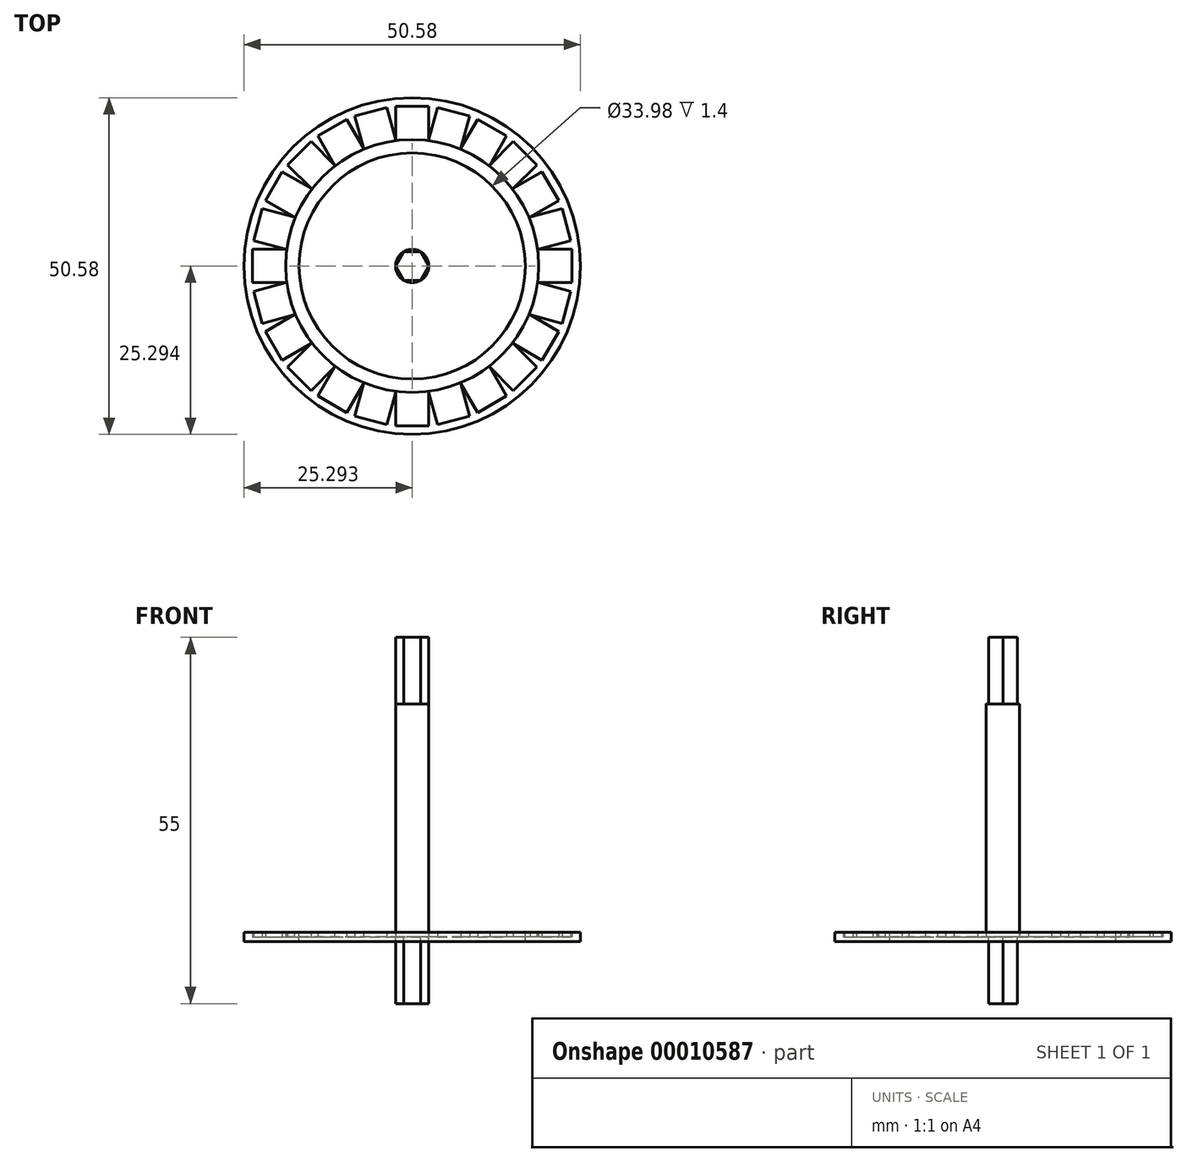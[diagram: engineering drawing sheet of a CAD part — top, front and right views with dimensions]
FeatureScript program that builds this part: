
annotation { "Feature Type Name" : "Feature", "Feature Type Description" : "" }
export const myFeature = defineFeature(function(context is Context, id is Id, definition is map)
    precondition{}
    {
        {
            var Q0;
            Q0=qCreatedBy(makeId("Top.planeOp"),FACE);
            var sketch = newSketch(context, id + "F0", { "sketchPlane" : qUnion([Q0])});
            skCircle(sketch, "E0", {"center": v(-14.89, 0.25) * mm, "radius": 18.99 * mm});
            skPoint(sketch, "E1", {"position": v(-14.89, 19.24) * mm});
            skLineSegment(sketch, "E2.bottom", {"start": v(-17.39, 24.24) * mm, "end": v(-12.39, 24.24) * mm});
            skLineSegment(sketch, "E2.top", {"start": v(-17.39, 19.24) * mm, "end": v(-12.39, 19.24) * mm});
            skLineSegment(sketch, "E2.left", {"start": v(-17.39, 24.24) * mm, "end": v(-17.39, 19.24) * mm});
            skLineSegment(sketch, "E2.right", {"start": v(-12.39, 24.24) * mm, "end": v(-12.39, 19.24) * mm});
            skPoint(sketch, "E3.1.0", {"position": v(-16.97, 18.97) * mm});
            skPoint(sketch, "E3.2.0", {"position": v(-18.92, 18.16) * mm});
            skPoint(sketch, "E3.3.0", {"position": v(-20.59, 16.88) * mm});
            skPoint(sketch, "E3.4.0", {"position": v(-21.87, 15.21) * mm});
            skPoint(sketch, "E3.5.0", {"position": v(-22.67, 13.27) * mm});
            skPoint(sketch, "E3.6.0", {"position": v(-22.95, 11.18) * mm});
            skPoint(sketch, "E3.7.0", {"position": v(-22.67, 9.1) * mm});
            skPoint(sketch, "E3.8.0", {"position": v(-21.87, 7.15) * mm});
            skPoint(sketch, "E3.9.0", {"position": v(-20.59, 5.48) * mm});
            skPoint(sketch, "E3.10.0", {"position": v(-18.92, 4.2) * mm});
            skPoint(sketch, "E3.11.0", {"position": v(-16.97, 3.4) * mm});
            skPoint(sketch, "E3.12.0", {"position": v(-14.89, 3.12) * mm});
            skPoint(sketch, "E3.13.0", {"position": v(-12.8, 3.4) * mm});
            skPoint(sketch, "E3.14.0", {"position": v(-10.86, 4.2) * mm});
            skPoint(sketch, "E3.15.0", {"position": v(-9.19, 5.48) * mm});
            skPoint(sketch, "E3.16.0", {"position": v(-7.9, 7.15) * mm});
            skPoint(sketch, "E3.17.0", {"position": v(-7.1, 9.1) * mm});
            skPoint(sketch, "E3.18.0", {"position": v(-6.82, 11.18) * mm});
            skPoint(sketch, "E3.19.0", {"position": v(-7.1, 13.27) * mm});
            skPoint(sketch, "E3.20.0", {"position": v(-7.9, 15.21) * mm});
            skPoint(sketch, "E3.21.0", {"position": v(-9.19, 16.88) * mm});
            skPoint(sketch, "E3.22.0", {"position": v(-10.86, 18.16) * mm});
            skPoint(sketch, "E3.23.0", {"position": v(-12.8, 18.97) * mm});
            skPoint(sketch, "E3.center", {"position": v(-14.89, 11.18) * mm});
            skLineSegment(sketch, "E4.1.0", {"start": v(-23.51, 22.78) * mm, "end": v(-22.22, 17.95) * mm});
            skLineSegment(sketch, "E4.1.1", {"start": v(-18.68, 24.07) * mm, "end": v(-17.39, 19.24) * mm});
            skLineSegment(sketch, "E4.1.2", {"start": v(-23.51, 22.78) * mm, "end": v(-18.68, 24.07) * mm});
            skLineSegment(sketch, "E4.1.3", {"start": v(-22.22, 17.95) * mm, "end": v(-17.39, 19.24) * mm});
            skLineSegment(sketch, "E4.2.0", {"start": v(-29.05, 19.78) * mm, "end": v(-26.55, 15.45) * mm});
            skLineSegment(sketch, "E4.2.1", {"start": v(-24.72, 22.28) * mm, "end": v(-22.22, 17.95) * mm});
            skLineSegment(sketch, "E4.2.2", {"start": v(-29.05, 19.78) * mm, "end": v(-24.72, 22.28) * mm});
            skLineSegment(sketch, "E4.2.3", {"start": v(-26.55, 15.45) * mm, "end": v(-22.22, 17.95) * mm});
            skLineSegment(sketch, "E4.3.0", {"start": v(-33.62, 15.45) * mm, "end": v(-30.08, 11.91) * mm});
            skLineSegment(sketch, "E4.3.1", {"start": v(-30.08, 18.98) * mm, "end": v(-26.55, 15.45) * mm});
            skLineSegment(sketch, "E4.3.2", {"start": v(-33.62, 15.45) * mm, "end": v(-30.08, 18.98) * mm});
            skLineSegment(sketch, "E4.3.3", {"start": v(-30.08, 11.91) * mm, "end": v(-26.55, 15.45) * mm});
            skLineSegment(sketch, "E4.4.0", {"start": v(-36.91, 10.08) * mm, "end": v(-32.58, 7.58) * mm});
            skLineSegment(sketch, "E4.4.1", {"start": v(-34.41, 14.41) * mm, "end": v(-30.08, 11.91) * mm});
            skLineSegment(sketch, "E4.4.2", {"start": v(-36.91, 10.08) * mm, "end": v(-34.41, 14.41) * mm});
            skLineSegment(sketch, "E4.4.3", {"start": v(-32.58, 7.58) * mm, "end": v(-30.08, 11.91) * mm});
            skLineSegment(sketch, "E4.5.0", {"start": v(-38.7, 4.05) * mm, "end": v(-33.88, 2.75) * mm});
            skLineSegment(sketch, "E4.5.1", {"start": v(-37.41, 8.88) * mm, "end": v(-32.58, 7.58) * mm});
            skLineSegment(sketch, "E4.5.2", {"start": v(-38.7, 4.05) * mm, "end": v(-37.41, 8.88) * mm});
            skLineSegment(sketch, "E4.5.3", {"start": v(-33.88, 2.75) * mm, "end": v(-32.58, 7.58) * mm});
            skLineSegment(sketch, "E4.6.0", {"start": v(-38.88, -2.25) * mm, "end": v(-33.88, -2.25) * mm});
            skLineSegment(sketch, "E4.6.1", {"start": v(-38.88, 2.75) * mm, "end": v(-33.88, 2.75) * mm});
            skLineSegment(sketch, "E4.6.2", {"start": v(-38.88, -2.25) * mm, "end": v(-38.88, 2.75) * mm});
            skLineSegment(sketch, "E4.6.3", {"start": v(-33.88, -2.25) * mm, "end": v(-33.88, 2.75) * mm});
            skLineSegment(sketch, "E4.7.0", {"start": v(-37.41, -8.37) * mm, "end": v(-32.58, -7.08) * mm});
            skLineSegment(sketch, "E4.7.1", {"start": v(-38.7, -3.54) * mm, "end": v(-33.88, -2.25) * mm});
            skLineSegment(sketch, "E4.7.2", {"start": v(-37.41, -8.37) * mm, "end": v(-38.7, -3.54) * mm});
            skLineSegment(sketch, "E4.7.3", {"start": v(-32.58, -7.08) * mm, "end": v(-33.88, -2.25) * mm});
            skLineSegment(sketch, "E4.8.0", {"start": v(-34.41, -13.9) * mm, "end": v(-30.08, -11.4) * mm});
            skLineSegment(sketch, "E4.8.1", {"start": v(-36.91, -9.58) * mm, "end": v(-32.58, -7.08) * mm});
            skLineSegment(sketch, "E4.8.2", {"start": v(-34.41, -13.9) * mm, "end": v(-36.91, -9.58) * mm});
            skLineSegment(sketch, "E4.8.3", {"start": v(-30.08, -11.4) * mm, "end": v(-32.58, -7.08) * mm});
            skLineSegment(sketch, "E4.9.0", {"start": v(-30.08, -18.48) * mm, "end": v(-26.55, -14.94) * mm});
            skLineSegment(sketch, "E4.9.1", {"start": v(-33.62, -14.94) * mm, "end": v(-30.08, -11.4) * mm});
            skLineSegment(sketch, "E4.9.2", {"start": v(-30.08, -18.48) * mm, "end": v(-33.62, -14.94) * mm});
            skLineSegment(sketch, "E4.9.3", {"start": v(-26.55, -14.94) * mm, "end": v(-30.08, -11.4) * mm});
            skLineSegment(sketch, "E4.10.0", {"start": v(-24.72, -21.77) * mm, "end": v(-22.22, -17.44) * mm});
            skLineSegment(sketch, "E4.10.1", {"start": v(-29.05, -19.27) * mm, "end": v(-26.55, -14.94) * mm});
            skLineSegment(sketch, "E4.10.2", {"start": v(-24.72, -21.77) * mm, "end": v(-29.05, -19.27) * mm});
            skLineSegment(sketch, "E4.10.3", {"start": v(-22.22, -17.44) * mm, "end": v(-26.55, -14.94) * mm});
            skLineSegment(sketch, "E4.11.0", {"start": v(-18.68, -23.57) * mm, "end": v(-17.39, -18.74) * mm});
            skLineSegment(sketch, "E4.11.1", {"start": v(-23.51, -22.27) * mm, "end": v(-22.22, -17.44) * mm});
            skLineSegment(sketch, "E4.11.2", {"start": v(-18.68, -23.57) * mm, "end": v(-23.51, -22.27) * mm});
            skLineSegment(sketch, "E4.11.3", {"start": v(-17.39, -18.74) * mm, "end": v(-22.22, -17.44) * mm});
            skLineSegment(sketch, "E4.12.0", {"start": v(-12.39, -23.74) * mm, "end": v(-12.39, -18.74) * mm});
            skLineSegment(sketch, "E4.12.1", {"start": v(-17.39, -23.74) * mm, "end": v(-17.39, -18.74) * mm});
            skLineSegment(sketch, "E4.12.2", {"start": v(-12.39, -23.74) * mm, "end": v(-17.39, -23.74) * mm});
            skLineSegment(sketch, "E4.12.3", {"start": v(-12.39, -18.74) * mm, "end": v(-17.39, -18.74) * mm});
            skLineSegment(sketch, "E4.13.0", {"start": v(-6.26, -22.27) * mm, "end": v(-7.56, -17.44) * mm});
            skLineSegment(sketch, "E4.13.1", {"start": v(-11.1, -23.57) * mm, "end": v(-12.39, -18.74) * mm});
            skLineSegment(sketch, "E4.13.2", {"start": v(-6.26, -22.27) * mm, "end": v(-11.1, -23.57) * mm});
            skLineSegment(sketch, "E4.13.3", {"start": v(-7.56, -17.44) * mm, "end": v(-12.39, -18.74) * mm});
            skLineSegment(sketch, "E4.14.0", {"start": v(-0.73, -19.27) * mm, "end": v(-3.23, -14.94) * mm});
            skLineSegment(sketch, "E4.14.1", {"start": v(-5.06, -21.77) * mm, "end": v(-7.56, -17.44) * mm});
            skLineSegment(sketch, "E4.14.2", {"start": v(-0.73, -19.27) * mm, "end": v(-5.06, -21.77) * mm});
            skLineSegment(sketch, "E4.14.3", {"start": v(-3.23, -14.94) * mm, "end": v(-7.56, -17.44) * mm});
            skLineSegment(sketch, "E4.15.0", {"start": v(3.84, -14.94) * mm, "end": v(0.3, -11.4) * mm});
            skLineSegment(sketch, "E4.15.1", {"start": v(0.3, -18.48) * mm, "end": v(-3.23, -14.94) * mm});
            skLineSegment(sketch, "E4.15.2", {"start": v(3.84, -14.94) * mm, "end": v(0.3, -18.48) * mm});
            skLineSegment(sketch, "E4.15.3", {"start": v(0.3, -11.4) * mm, "end": v(-3.23, -14.94) * mm});
            skLineSegment(sketch, "E4.16.0", {"start": v(7.14, -9.58) * mm, "end": v(2.8, -7.08) * mm});
            skLineSegment(sketch, "E4.16.1", {"start": v(4.64, -13.9) * mm, "end": v(0.3, -11.4) * mm});
            skLineSegment(sketch, "E4.16.2", {"start": v(7.14, -9.58) * mm, "end": v(4.64, -13.9) * mm});
            skLineSegment(sketch, "E4.16.3", {"start": v(2.8, -7.08) * mm, "end": v(0.3, -11.4) * mm});
            skLineSegment(sketch, "E4.17.0", {"start": v(8.93, -3.54) * mm, "end": v(4.1, -2.25) * mm});
            skLineSegment(sketch, "E4.17.1", {"start": v(7.64, -8.37) * mm, "end": v(2.8, -7.08) * mm});
            skLineSegment(sketch, "E4.17.2", {"start": v(8.93, -3.54) * mm, "end": v(7.64, -8.37) * mm});
            skLineSegment(sketch, "E4.17.3", {"start": v(4.1, -2.25) * mm, "end": v(2.8, -7.08) * mm});
            skLineSegment(sketch, "E4.18.0", {"start": v(9.1, 2.75) * mm, "end": v(4.1, 2.75) * mm});
            skLineSegment(sketch, "E4.18.1", {"start": v(9.1, -2.25) * mm, "end": v(4.1, -2.25) * mm});
            skLineSegment(sketch, "E4.18.2", {"start": v(9.1, 2.75) * mm, "end": v(9.1, -2.25) * mm});
            skLineSegment(sketch, "E4.18.3", {"start": v(4.1, 2.75) * mm, "end": v(4.1, -2.25) * mm});
            skLineSegment(sketch, "E4.19.0", {"start": v(7.64, 8.88) * mm, "end": v(2.8, 7.58) * mm});
            skLineSegment(sketch, "E4.19.1", {"start": v(8.93, 4.05) * mm, "end": v(4.1, 2.75) * mm});
            skLineSegment(sketch, "E4.19.2", {"start": v(7.64, 8.88) * mm, "end": v(8.93, 4.05) * mm});
            skLineSegment(sketch, "E4.19.3", {"start": v(2.8, 7.58) * mm, "end": v(4.1, 2.75) * mm});
            skLineSegment(sketch, "E4.20.0", {"start": v(4.64, 14.41) * mm, "end": v(0.3, 11.91) * mm});
            skLineSegment(sketch, "E4.20.1", {"start": v(7.14, 10.08) * mm, "end": v(2.8, 7.58) * mm});
            skLineSegment(sketch, "E4.20.2", {"start": v(4.64, 14.41) * mm, "end": v(7.14, 10.08) * mm});
            skLineSegment(sketch, "E4.20.3", {"start": v(0.3, 11.91) * mm, "end": v(2.8, 7.58) * mm});
            skLineSegment(sketch, "E4.21.0", {"start": v(0.3, 18.98) * mm, "end": v(-3.23, 15.45) * mm});
            skLineSegment(sketch, "E4.21.1", {"start": v(3.84, 15.45) * mm, "end": v(0.3, 11.91) * mm});
            skLineSegment(sketch, "E4.21.2", {"start": v(0.3, 18.98) * mm, "end": v(3.84, 15.45) * mm});
            skLineSegment(sketch, "E4.21.3", {"start": v(-3.23, 15.45) * mm, "end": v(0.3, 11.91) * mm});
            skLineSegment(sketch, "E4.22.0", {"start": v(-5.06, 22.28) * mm, "end": v(-7.56, 17.95) * mm});
            skLineSegment(sketch, "E4.22.1", {"start": v(-0.73, 19.78) * mm, "end": v(-3.23, 15.45) * mm});
            skLineSegment(sketch, "E4.22.2", {"start": v(-5.06, 22.28) * mm, "end": v(-0.73, 19.78) * mm});
            skLineSegment(sketch, "E4.22.3", {"start": v(-7.56, 17.95) * mm, "end": v(-3.23, 15.45) * mm});
            skLineSegment(sketch, "E4.23.0", {"start": v(-11.1, 24.07) * mm, "end": v(-12.39, 19.24) * mm});
            skLineSegment(sketch, "E4.23.1", {"start": v(-6.26, 22.78) * mm, "end": v(-7.56, 17.95) * mm});
            skLineSegment(sketch, "E4.23.2", {"start": v(-11.1, 24.07) * mm, "end": v(-6.26, 22.78) * mm});
            skLineSegment(sketch, "E4.23.3", {"start": v(-12.39, 19.24) * mm, "end": v(-7.56, 17.95) * mm});
            skPoint(sketch, "E5", {"position": v(-38.88, 0.25) * mm});
            skPoint(sketch, "E6", {"position": v(9.1, 0.25) * mm});
            skCircle(sketch, "E7", {"center": v(-14.89, 0.25) * mm, "radius": 23.99 * mm});
            skCircle(sketch, "E8.0", {"center": v(-14.89, 0.25) * mm, "radius": 25.29 * mm});
            skCircle(sketch, "E9.0", {"center": v(-14.89, 0.25) * mm, "radius": 16.99 * mm});
            skLineSegment(sketch, "E10", {"start": v(-14.89, 3.12) * mm, "end": v(-14.89, 19.24) * mm});
            skCircle(sketch, "E11.cCircle", {"center": v(-14.89, 0.25) * mm, "radius": 2.17 * mm, "construction": true});
            skLineSegment(sketch, "E11.0", {"start": v(-13.64, -1.91) * mm, "end": v(-16.14, -1.91) * mm});
            skLineSegment(sketch, "E11.1", {"start": v(-16.14, -1.91) * mm, "end": v(-17.39, 0.25) * mm});
            skLineSegment(sketch, "E11.2", {"start": v(-17.39, 0.25) * mm, "end": v(-16.14, 2.42) * mm});
            skLineSegment(sketch, "E11.3", {"start": v(-16.14, 2.42) * mm, "end": v(-13.64, 2.42) * mm});
            skLineSegment(sketch, "E11.4", {"start": v(-13.64, 2.42) * mm, "end": v(-12.39, 0.25) * mm});
            skLineSegment(sketch, "E11.5", {"start": v(-12.39, 0.25) * mm, "end": v(-13.64, -1.91) * mm});
            skPoint(sketch, "E11.0.midPoint", {"position": v(-14.89, -1.91) * mm});
            skLineSegment(sketch, "E12.bottom", {"start": v(-40.18, 25.54) * mm, "end": v(10.4, 25.54) * mm});
            skLineSegment(sketch, "E12.top", {"start": v(-40.18, -25.04) * mm, "end": v(10.4, -25.04) * mm});
            skLineSegment(sketch, "E12.left", {"start": v(-40.18, 25.54) * mm, "end": v(-40.18, -25.04) * mm});
            skLineSegment(sketch, "E12.right", {"start": v(10.4, 25.54) * mm, "end": v(10.4, -25.04) * mm});
            skCircle(sketch, "E13", {"center": v(-14.89, 0.25) * mm, "radius": 2.5 * mm});
            skCircle(sketch, "E14.0", {"center": v(-14.89, 0.25) * mm, "radius": 26.79 * mm});
            skCircle(sketch, "E15", {"center": v(-40.18, 25.54) * mm, "radius": 1 * mm});
            skCircle(sketch, "E16", {"center": v(10.4, 25.54) * mm, "radius": 1 * mm});
            skCircle(sketch, "E17", {"center": v(-40.18, -25.04) * mm, "radius": 1 * mm});
            skCircle(sketch, "E18", {"center": v(10.4, -25.04) * mm, "radius": 1 * mm});
            skCircle(sketch, "E19.0", {"center": v(-40.18, 25.54) * mm, "radius": 3 * mm});
            skCircle(sketch, "E20", {"center": v(10.4, 25.54) * mm, "radius": 3 * mm});
            skCircle(sketch, "E21", {"center": v(10.4, -25.04) * mm, "radius": 3 * mm});
            skCircle(sketch, "E22", {"center": v(-40.18, -25.04) * mm, "radius": 3 * mm});
            skEllipse(sketch, "E23", {"center": v(-14.89, 11.18) * mm, "majorRadius": 6.02 * mm, "minorRadius": 3.34 * mm, "majorAxis": v(0, -1)});
            skEllipse(sketch, "E24.1.0", {"center": v(-23.43, 7.07) * mm, "majorRadius": 6.02 * mm, "minorRadius": 3.34 * mm, "majorAxis": v(0.78, -0.62)});
            skEllipse(sketch, "E24.2.0", {"center": v(-25.54, -2.18) * mm, "majorRadius": 6.02 * mm, "minorRadius": 3.34 * mm, "majorAxis": v(0.97, 0.22)});
            skEllipse(sketch, "E24.3.0", {"center": v(-19.63, -9.6) * mm, "majorRadius": 6.02 * mm, "minorRadius": 3.34 * mm, "majorAxis": v(0.43, 0.9)});
            skEllipse(sketch, "E24.4.0", {"center": v(-10.15, -9.6) * mm, "majorRadius": 6.02 * mm, "minorRadius": 3.34 * mm, "majorAxis": v(-0.43, 0.9)});
            skEllipse(sketch, "E24.5.0", {"center": v(-4.23, -2.18) * mm, "majorRadius": 6.02 * mm, "minorRadius": 3.34 * mm, "majorAxis": v(-0.97, 0.22)});
            skEllipse(sketch, "E24.6.0", {"center": v(-6.34, 7.07) * mm, "majorRadius": 6.02 * mm, "minorRadius": 3.34 * mm, "majorAxis": v(-0.78, -0.62)});
            skSolve(sketch);
        }
        {
            var Q0;
            Q0=makeQuery(id+"F0.imprint","IMPRINT",FACE,{"disambiguationData":[TD([[makeQuery(id+"F0.imprint","IMPRINT",EDGE,{"derivedFrom":sQuery(id+"F0.wireOp",EDGE,"E9.0")}),-1.0]])]});
            var Q1;
            {var subQ40=sQuery(id+"F0.wireOp",EDGE,"E2.left");var subQ122=sQuery(id+"F0.wireOp",EDGE,"E2.bottom");var subQ171=makeQuery(id+"F0.imprint","INTERSECT",VERTEX,{"derivedFrom":[subQ122,subQ40]});Q1=makeQuery(id+"F0.imprint","IMPRINT",FACE,{"disambiguationData":[TD([[makeQuery(id+"F0.imprint","IMPRINT",EDGE,{"disambiguationData":[TD([[subQ171,-1.0]])],"derivedFrom":subQ122}),1.0]])]});}
            var Q2;
            {var subQ0=sQuery(id+"F0.wireOp",EDGE,"E7");var subQ4=sQuery(id+"F0.wireOp",EDGE,"E4.12.1");var subQ5=makeQuery(id+"F0.imprint","INTERSECT",VERTEX,{"derivedFrom":[subQ4,subQ0]});Q2=makeQuery(id+"F0.imprint","IMPRINT",FACE,{"disambiguationData":[TD([[makeQuery(id+"F0.imprint","IMPRINT",EDGE,{"disambiguationData":[TD([[subQ5,-1.0]])],"derivedFrom":subQ0}),1.0]])]});}
            var Q3;
            {var subQ0=sQuery(id+"F0.wireOp",EDGE,"E7");var subQ4=sQuery(id+"F0.wireOp",EDGE,"E4.11.1");var subQ5=makeQuery(id+"F0.imprint","INTERSECT",VERTEX,{"derivedFrom":[subQ4,subQ0]});Q3=makeQuery(id+"F0.imprint","IMPRINT",FACE,{"disambiguationData":[TD([[makeQuery(id+"F0.imprint","IMPRINT",EDGE,{"disambiguationData":[TD([[subQ5,-1.0]])],"derivedFrom":subQ0}),1.0]])]});}
            var Q4;
            {var subQ0=sQuery(id+"F0.wireOp",EDGE,"E7");var subQ4=sQuery(id+"F0.wireOp",EDGE,"E4.13.1");var subQ5=makeQuery(id+"F0.imprint","INTERSECT",VERTEX,{"derivedFrom":[subQ4,subQ0]});Q4=makeQuery(id+"F0.imprint","IMPRINT",FACE,{"disambiguationData":[TD([[makeQuery(id+"F0.imprint","IMPRINT",EDGE,{"disambiguationData":[TD([[subQ5,-1.0]])],"derivedFrom":subQ0}),1.0]])]});}
            var Q5;
            {var subQ0=sQuery(id+"F0.wireOp",EDGE,"E7");var subQ4=sQuery(id+"F0.wireOp",EDGE,"E4.10.1");var subQ5=makeQuery(id+"F0.imprint","INTERSECT",VERTEX,{"derivedFrom":[subQ4,subQ0]});Q5=makeQuery(id+"F0.imprint","IMPRINT",FACE,{"disambiguationData":[TD([[makeQuery(id+"F0.imprint","IMPRINT",EDGE,{"disambiguationData":[TD([[subQ5,-1.0]])],"derivedFrom":subQ0}),1.0]])]});}
            var Q6;
            {var subQ0=sQuery(id+"F0.wireOp",EDGE,"E7");var subQ4=sQuery(id+"F0.wireOp",EDGE,"E4.14.1");var subQ5=makeQuery(id+"F0.imprint","INTERSECT",VERTEX,{"derivedFrom":[subQ4,subQ0]});Q6=makeQuery(id+"F0.imprint","IMPRINT",FACE,{"disambiguationData":[TD([[makeQuery(id+"F0.imprint","IMPRINT",EDGE,{"disambiguationData":[TD([[subQ5,-1.0]])],"derivedFrom":subQ0}),1.0]])]});}
            var Q7;
            {var subQ0=sQuery(id+"F0.wireOp",EDGE,"E7");var subQ3=sQuery(id+"F0.wireOp",EDGE,"E4.9.0");var subQ4=makeQuery(id+"F0.imprint","INTERSECT",VERTEX,{"derivedFrom":[subQ3,subQ0]});Q7=makeQuery(id+"F0.imprint","IMPRINT",FACE,{"disambiguationData":[TD([[makeQuery(id+"F0.imprint","IMPRINT",EDGE,{"disambiguationData":[TD([[subQ4,-1.0]])],"derivedFrom":subQ0}),1.0]])]});}
            var Q8;
            {var subQ0=sQuery(id+"F0.wireOp",EDGE,"E7");var subQ3=sQuery(id+"F0.wireOp",EDGE,"E4.14.0");var subQ4=makeQuery(id+"F0.imprint","INTERSECT",VERTEX,{"derivedFrom":[subQ3,subQ0]});Q8=makeQuery(id+"F0.imprint","IMPRINT",FACE,{"disambiguationData":[TD([[makeQuery(id+"F0.imprint","IMPRINT",EDGE,{"disambiguationData":[TD([[subQ4,-1.0]])],"derivedFrom":subQ0}),1.0]])]});}
            var Q9;
            {var subQ0=sQuery(id+"F0.wireOp",EDGE,"E7");var subQ2=sQuery(id+"F0.wireOp",EDGE,"E4.9.1");var subQ3=makeQuery(id+"F0.imprint","INTERSECT",VERTEX,{"derivedFrom":[subQ2,subQ0]});Q9=makeQuery(id+"F0.imprint","IMPRINT",FACE,{"disambiguationData":[TD([[makeQuery(id+"F0.imprint","IMPRINT",EDGE,{"disambiguationData":[TD([[subQ3,-1.0]])],"derivedFrom":subQ0}),1.0]])]});}
            var Q10;
            {var subQ0=sQuery(id+"F0.wireOp",EDGE,"E7");var subQ4=sQuery(id+"F0.wireOp",EDGE,"E4.15.1");var subQ5=makeQuery(id+"F0.imprint","INTERSECT",VERTEX,{"derivedFrom":[subQ4,subQ0]});Q10=makeQuery(id+"F0.imprint","IMPRINT",FACE,{"disambiguationData":[TD([[makeQuery(id+"F0.imprint","IMPRINT",EDGE,{"disambiguationData":[TD([[subQ5,-1.0]])],"derivedFrom":subQ0}),1.0]])]});}
            var Q11;
            {var subQ0=sQuery(id+"F0.wireOp",EDGE,"E7");var subQ3=sQuery(id+"F0.wireOp",EDGE,"E4.15.0");var subQ4=makeQuery(id+"F0.imprint","INTERSECT",VERTEX,{"derivedFrom":[subQ3,subQ0]});Q11=makeQuery(id+"F0.imprint","IMPRINT",FACE,{"disambiguationData":[TD([[makeQuery(id+"F0.imprint","IMPRINT",EDGE,{"disambiguationData":[TD([[subQ4,-1.0]])],"derivedFrom":subQ0}),1.0]])]});}
            var Q12;
            {var subQ0=sQuery(id+"F0.wireOp",EDGE,"E7");var subQ6=sQuery(id+"F0.wireOp",EDGE,"E4.8.1");var subQ9=makeQuery(id+"F0.imprint","INTERSECT",VERTEX,{"derivedFrom":[subQ6,subQ0]});Q12=makeQuery(id+"F0.imprint","IMPRINT",FACE,{"disambiguationData":[TD([[makeQuery(id+"F0.imprint","IMPRINT",EDGE,{"disambiguationData":[TD([[subQ9,-1.0]])],"derivedFrom":subQ0}),1.0]])]});}
            var Q13;
            {var subQ0=sQuery(id+"F0.wireOp",EDGE,"E7");var subQ4=sQuery(id+"F0.wireOp",EDGE,"E4.16.1");var subQ5=makeQuery(id+"F0.imprint","INTERSECT",VERTEX,{"derivedFrom":[subQ4,subQ0]});Q13=makeQuery(id+"F0.imprint","IMPRINT",FACE,{"disambiguationData":[TD([[makeQuery(id+"F0.imprint","IMPRINT",EDGE,{"disambiguationData":[TD([[subQ5,-1.0]])],"derivedFrom":subQ0}),1.0]])]});}
            var Q14;
            {var subQ0=sQuery(id+"F0.wireOp",EDGE,"E7");var subQ3=sQuery(id+"F0.wireOp",EDGE,"E4.16.0");var subQ4=makeQuery(id+"F0.imprint","INTERSECT",VERTEX,{"derivedFrom":[subQ3,subQ0]});Q14=makeQuery(id+"F0.imprint","IMPRINT",FACE,{"disambiguationData":[TD([[makeQuery(id+"F0.imprint","IMPRINT",EDGE,{"disambiguationData":[TD([[subQ4,-1.0]])],"derivedFrom":subQ0}),1.0]])]});}
            var Q15;
            {var subQ0=sQuery(id+"F0.wireOp",EDGE,"E7");var subQ4=sQuery(id+"F0.wireOp",EDGE,"E4.7.1");var subQ5=makeQuery(id+"F0.imprint","INTERSECT",VERTEX,{"derivedFrom":[subQ4,subQ0]});Q15=makeQuery(id+"F0.imprint","IMPRINT",FACE,{"disambiguationData":[TD([[makeQuery(id+"F0.imprint","IMPRINT",EDGE,{"disambiguationData":[TD([[subQ5,-1.0]])],"derivedFrom":subQ0}),1.0]])]});}
            var Q16;
            {var subQ0=sQuery(id+"F0.wireOp",EDGE,"E7");var subQ6=sQuery(id+"F0.wireOp",EDGE,"E4.17.1");var subQ8=makeQuery(id+"F0.imprint","INTERSECT",VERTEX,{"derivedFrom":[subQ6,subQ0]});Q16=makeQuery(id+"F0.imprint","IMPRINT",FACE,{"disambiguationData":[TD([[makeQuery(id+"F0.imprint","IMPRINT",EDGE,{"disambiguationData":[TD([[subQ8,-1.0]])],"derivedFrom":subQ0}),1.0]])]});}
            var Q17;
            {var subQ0=sQuery(id+"F0.wireOp",EDGE,"E7");var subQ3=sQuery(id+"F0.wireOp",EDGE,"E4.6.0");var subQ4=makeQuery(id+"F0.imprint","INTERSECT",VERTEX,{"derivedFrom":[subQ3,subQ0]});Q17=makeQuery(id+"F0.imprint","IMPRINT",FACE,{"disambiguationData":[TD([[makeQuery(id+"F0.imprint","IMPRINT",EDGE,{"disambiguationData":[TD([[subQ4,-1.0]])],"derivedFrom":subQ0}),1.0]])]});}
            var Q18;
            {var subQ0=sQuery(id+"F0.wireOp",EDGE,"E7");var subQ3=sQuery(id+"F0.wireOp",EDGE,"E4.17.0");var subQ4=makeQuery(id+"F0.imprint","INTERSECT",VERTEX,{"derivedFrom":[subQ3,subQ0]});Q18=makeQuery(id+"F0.imprint","IMPRINT",FACE,{"disambiguationData":[TD([[makeQuery(id+"F0.imprint","IMPRINT",EDGE,{"disambiguationData":[TD([[subQ4,-1.0]])],"derivedFrom":subQ0}),1.0]])]});}
            var Q19;
            {var subQ0=sQuery(id+"F0.wireOp",EDGE,"E7");var subQ4=sQuery(id+"F0.wireOp",EDGE,"E4.6.1");var subQ5=makeQuery(id+"F0.imprint","INTERSECT",VERTEX,{"derivedFrom":[subQ4,subQ0]});Q19=makeQuery(id+"F0.imprint","IMPRINT",FACE,{"disambiguationData":[TD([[makeQuery(id+"F0.imprint","IMPRINT",EDGE,{"disambiguationData":[TD([[subQ5,-1.0]])],"derivedFrom":subQ0}),1.0]])]});}
            var Q20;
            {var subQ0=sQuery(id+"F0.wireOp",EDGE,"E7");var subQ4=sQuery(id+"F0.wireOp",EDGE,"E4.18.0");var subQ5=makeQuery(id+"F0.imprint","INTERSECT",VERTEX,{"derivedFrom":[subQ4,subQ0]});Q20=makeQuery(id+"F0.imprint","IMPRINT",FACE,{"disambiguationData":[TD([[makeQuery(id+"F0.imprint","IMPRINT",EDGE,{"disambiguationData":[TD([[subQ5,1.0]])],"derivedFrom":subQ0}),1.0]])]});}
            var Q21;
            {var subQ0=sQuery(id+"F0.wireOp",EDGE,"E7");var subQ4=sQuery(id+"F0.wireOp",EDGE,"E4.5.1");var subQ5=makeQuery(id+"F0.imprint","INTERSECT",VERTEX,{"derivedFrom":[subQ4,subQ0]});Q21=makeQuery(id+"F0.imprint","IMPRINT",FACE,{"disambiguationData":[TD([[makeQuery(id+"F0.imprint","IMPRINT",EDGE,{"disambiguationData":[TD([[subQ5,-1.0]])],"derivedFrom":subQ0}),1.0]])]});}
            var Q22;
            {var subQ0=sQuery(id+"F0.wireOp",EDGE,"E7");var subQ4=sQuery(id+"F0.wireOp",EDGE,"E4.19.1");var subQ5=makeQuery(id+"F0.imprint","INTERSECT",VERTEX,{"derivedFrom":[subQ4,subQ0]});Q22=makeQuery(id+"F0.imprint","IMPRINT",FACE,{"disambiguationData":[TD([[makeQuery(id+"F0.imprint","IMPRINT",EDGE,{"disambiguationData":[TD([[subQ5,-1.0]])],"derivedFrom":subQ0}),1.0]])]});}
            var Q23;
            {var subQ0=sQuery(id+"F0.wireOp",EDGE,"E7");var subQ3=sQuery(id+"F0.wireOp",EDGE,"E4.4.0");var subQ4=makeQuery(id+"F0.imprint","INTERSECT",VERTEX,{"derivedFrom":[subQ3,subQ0]});Q23=makeQuery(id+"F0.imprint","IMPRINT",FACE,{"disambiguationData":[TD([[makeQuery(id+"F0.imprint","IMPRINT",EDGE,{"disambiguationData":[TD([[subQ4,-1.0]])],"derivedFrom":subQ0}),1.0]])]});}
            var Q24;
            {var subQ0=sQuery(id+"F0.wireOp",EDGE,"E7");var subQ4=sQuery(id+"F0.wireOp",EDGE,"E4.4.1");var subQ5=makeQuery(id+"F0.imprint","INTERSECT",VERTEX,{"derivedFrom":[subQ4,subQ0]});Q24=makeQuery(id+"F0.imprint","IMPRINT",FACE,{"disambiguationData":[TD([[makeQuery(id+"F0.imprint","IMPRINT",EDGE,{"disambiguationData":[TD([[subQ5,-1.0]])],"derivedFrom":subQ0}),1.0]])]});}
            var Q25;
            {var subQ0=sQuery(id+"F0.wireOp",EDGE,"E7");var subQ6=sQuery(id+"F0.wireOp",EDGE,"E4.20.1");var subQ9=makeQuery(id+"F0.imprint","INTERSECT",VERTEX,{"derivedFrom":[subQ6,subQ0]});Q25=makeQuery(id+"F0.imprint","IMPRINT",FACE,{"disambiguationData":[TD([[makeQuery(id+"F0.imprint","IMPRINT",EDGE,{"disambiguationData":[TD([[subQ9,-1.0]])],"derivedFrom":subQ0}),1.0]])]});}
            var Q26;
            {var subQ0=sQuery(id+"F0.wireOp",EDGE,"E7");var subQ3=sQuery(id+"F0.wireOp",EDGE,"E4.19.0");var subQ4=makeQuery(id+"F0.imprint","INTERSECT",VERTEX,{"derivedFrom":[subQ3,subQ0]});Q26=makeQuery(id+"F0.imprint","IMPRINT",FACE,{"disambiguationData":[TD([[makeQuery(id+"F0.imprint","IMPRINT",EDGE,{"disambiguationData":[TD([[subQ4,-1.0]])],"derivedFrom":subQ0}),1.0]])]});}
            var Q27;
            {var subQ0=sQuery(id+"F0.wireOp",EDGE,"E7");var subQ4=sQuery(id+"F0.wireOp",EDGE,"E4.3.1");var subQ5=makeQuery(id+"F0.imprint","INTERSECT",VERTEX,{"derivedFrom":[subQ4,subQ0]});Q27=makeQuery(id+"F0.imprint","IMPRINT",FACE,{"disambiguationData":[TD([[makeQuery(id+"F0.imprint","IMPRINT",EDGE,{"disambiguationData":[TD([[subQ5,-1.0]])],"derivedFrom":subQ0}),1.0]])]});}
            var Q28;
            {var subQ0=sQuery(id+"F0.wireOp",EDGE,"E7");var subQ4=sQuery(id+"F0.wireOp",EDGE,"E4.21.1");var subQ5=makeQuery(id+"F0.imprint","INTERSECT",VERTEX,{"derivedFrom":[subQ4,subQ0]});Q28=makeQuery(id+"F0.imprint","IMPRINT",FACE,{"disambiguationData":[TD([[makeQuery(id+"F0.imprint","IMPRINT",EDGE,{"disambiguationData":[TD([[subQ5,-1.0]])],"derivedFrom":subQ0}),1.0]])]});}
            var Q29;
            {var subQ0=sQuery(id+"F0.wireOp",EDGE,"E7");var subQ3=sQuery(id+"F0.wireOp",EDGE,"E4.3.0");var subQ4=makeQuery(id+"F0.imprint","INTERSECT",VERTEX,{"derivedFrom":[subQ3,subQ0]});Q29=makeQuery(id+"F0.imprint","IMPRINT",FACE,{"disambiguationData":[TD([[makeQuery(id+"F0.imprint","IMPRINT",EDGE,{"disambiguationData":[TD([[subQ4,-1.0]])],"derivedFrom":subQ0}),1.0]])]});}
            var Q30;
            {var subQ0=sQuery(id+"F0.wireOp",EDGE,"E7");var subQ3=sQuery(id+"F0.wireOp",EDGE,"E4.20.0");var subQ4=makeQuery(id+"F0.imprint","INTERSECT",VERTEX,{"derivedFrom":[subQ3,subQ0]});Q30=makeQuery(id+"F0.imprint","IMPRINT",FACE,{"disambiguationData":[TD([[makeQuery(id+"F0.imprint","IMPRINT",EDGE,{"disambiguationData":[TD([[subQ4,-1.0]])],"derivedFrom":subQ0}),1.0]])]});}
            var Q31;
            {var subQ0=sQuery(id+"F0.wireOp",EDGE,"E7");var subQ4=sQuery(id+"F0.wireOp",EDGE,"E4.2.1");var subQ5=makeQuery(id+"F0.imprint","INTERSECT",VERTEX,{"derivedFrom":[subQ4,subQ0]});Q31=makeQuery(id+"F0.imprint","IMPRINT",FACE,{"disambiguationData":[TD([[makeQuery(id+"F0.imprint","IMPRINT",EDGE,{"disambiguationData":[TD([[subQ5,-1.0]])],"derivedFrom":subQ0}),1.0]])]});}
            var Q32;
            {var subQ0=sQuery(id+"F0.wireOp",EDGE,"E7");var subQ4=sQuery(id+"F0.wireOp",EDGE,"E4.22.1");var subQ5=makeQuery(id+"F0.imprint","INTERSECT",VERTEX,{"derivedFrom":[subQ4,subQ0]});Q32=makeQuery(id+"F0.imprint","IMPRINT",FACE,{"disambiguationData":[TD([[makeQuery(id+"F0.imprint","IMPRINT",EDGE,{"disambiguationData":[TD([[subQ5,-1.0]])],"derivedFrom":subQ0}),1.0]])]});}
            var Q33;
            {var subQ0=sQuery(id+"F0.wireOp",EDGE,"E7");var subQ3=sQuery(id+"F0.wireOp",EDGE,"E4.2.0");var subQ4=makeQuery(id+"F0.imprint","INTERSECT",VERTEX,{"derivedFrom":[subQ3,subQ0]});Q33=makeQuery(id+"F0.imprint","IMPRINT",FACE,{"disambiguationData":[TD([[makeQuery(id+"F0.imprint","IMPRINT",EDGE,{"disambiguationData":[TD([[subQ4,-1.0]])],"derivedFrom":subQ0}),1.0]])]});}
            var Q34;
            {var subQ0=sQuery(id+"F0.wireOp",EDGE,"E7");var subQ4=sQuery(id+"F0.wireOp",EDGE,"E4.1.1");var subQ5=makeQuery(id+"F0.imprint","INTERSECT",VERTEX,{"derivedFrom":[subQ4,subQ0]});Q34=makeQuery(id+"F0.imprint","IMPRINT",FACE,{"disambiguationData":[TD([[makeQuery(id+"F0.imprint","IMPRINT",EDGE,{"disambiguationData":[TD([[subQ5,-1.0]])],"derivedFrom":subQ0}),1.0]])]});}
            var Q35;
            {var subQ0=sQuery(id+"F0.wireOp",EDGE,"E7");var subQ6=sQuery(id+"F0.wireOp",EDGE,"E4.23.1");var subQ8=makeQuery(id+"F0.imprint","INTERSECT",VERTEX,{"derivedFrom":[subQ6,subQ0]});Q35=makeQuery(id+"F0.imprint","IMPRINT",FACE,{"disambiguationData":[TD([[makeQuery(id+"F0.imprint","IMPRINT",EDGE,{"disambiguationData":[TD([[subQ8,-1.0]])],"derivedFrom":subQ0}),1.0]])]});}
            var Q36;
            {var subQ0=sQuery(id+"F0.wireOp",EDGE,"E7");var subQ3=makeQuery(id+"F0.imprint","INTERSECT",VERTEX,{"derivedFrom":[sQuery(id+"F0.wireOp",EDGE,"E2.bottom"),subQ0]});Q36=makeQuery(id+"F0.imprint","IMPRINT",FACE,{"disambiguationData":[TD([[makeQuery(id+"F0.imprint","IMPRINT",EDGE,{"disambiguationData":[TD([[subQ3,1.0]])],"derivedFrom":subQ0}),1.0]])]});}
            var Q37;
            {var subQ1=sQuery(id+"F0.wireOp",EDGE,"E0");var subQ3=sQuery(id+"F0.wireOp",EDGE,"E4.10.3");var subQ5=makeQuery(id+"F0.imprint","INTERSECT",VERTEX,{"derivedFrom":[subQ1,subQ3]});Q37=makeQuery(id+"F0.imprint","IMPRINT",FACE,{"disambiguationData":[TD([[makeQuery(id+"F0.imprint","IMPRINT",EDGE,{"disambiguationData":[TD([[subQ5,-1.0]])],"derivedFrom":subQ1}),-1.0]])]});}
            var Q38;
            {var subQ1=sQuery(id+"F0.wireOp",EDGE,"E4.6.2");var subQ3=sQuery(id+"F0.wireOp",EDGE,"E4.6.0");var subQ5=makeQuery(id+"F0.imprint","INTERSECT",VERTEX,{"derivedFrom":[subQ3,subQ1]});Q38=makeQuery(id+"F0.imprint","IMPRINT",FACE,{"disambiguationData":[TD([[makeQuery(id+"F0.imprint","IMPRINT",EDGE,{"disambiguationData":[TD([[subQ5,-1.0]])],"derivedFrom":subQ3}),1.0]])]});}
            var Q39;
            {var subQ1=sQuery(id+"F0.wireOp",EDGE,"E4.4.2");var subQ3=sQuery(id+"F0.wireOp",EDGE,"E4.4.1");var subQ5=makeQuery(id+"F0.imprint","INTERSECT",VERTEX,{"derivedFrom":[subQ3,subQ1]});Q39=makeQuery(id+"F0.imprint","IMPRINT",FACE,{"disambiguationData":[TD([[makeQuery(id+"F0.imprint","IMPRINT",EDGE,{"disambiguationData":[TD([[subQ5,-1.0]])],"derivedFrom":subQ3}),-1.0]])]});}
            var Q40;
            {var subQ1=sQuery(id+"F0.wireOp",EDGE,"E4.22.2");var subQ3=sQuery(id+"F0.wireOp",EDGE,"E4.22.0");var subQ5=makeQuery(id+"F0.imprint","INTERSECT",VERTEX,{"derivedFrom":[subQ3,subQ1]});Q40=makeQuery(id+"F0.imprint","IMPRINT",FACE,{"disambiguationData":[TD([[makeQuery(id+"F0.imprint","IMPRINT",EDGE,{"disambiguationData":[TD([[subQ5,-1.0]])],"derivedFrom":subQ3}),1.0]])]});}
            var Q41;
            {var subQ1=sQuery(id+"F0.wireOp",EDGE,"E4.1.2");var subQ3=sQuery(id+"F0.wireOp",EDGE,"E4.1.0");var subQ5=makeQuery(id+"F0.imprint","INTERSECT",VERTEX,{"derivedFrom":[subQ3,subQ1]});Q41=makeQuery(id+"F0.imprint","IMPRINT",FACE,{"disambiguationData":[TD([[makeQuery(id+"F0.imprint","IMPRINT",EDGE,{"disambiguationData":[TD([[subQ5,-1.0]])],"derivedFrom":subQ3}),1.0]])]});}
            var Q42;
            {var subQ1=sQuery(id+"F0.wireOp",EDGE,"E4.1.2");var subQ3=sQuery(id+"F0.wireOp",EDGE,"E4.1.1");var subQ5=makeQuery(id+"F0.imprint","INTERSECT",VERTEX,{"derivedFrom":[subQ3,subQ1]});Q42=makeQuery(id+"F0.imprint","IMPRINT",FACE,{"disambiguationData":[TD([[makeQuery(id+"F0.imprint","IMPRINT",EDGE,{"disambiguationData":[TD([[subQ5,-1.0]])],"derivedFrom":subQ3}),-1.0]])]});}
            var Q43;
            {var subQ1=sQuery(id+"F0.wireOp",EDGE,"E4.2.2");var subQ3=sQuery(id+"F0.wireOp",EDGE,"E4.2.0");var subQ5=makeQuery(id+"F0.imprint","INTERSECT",VERTEX,{"derivedFrom":[subQ3,subQ1]});Q43=makeQuery(id+"F0.imprint","IMPRINT",FACE,{"disambiguationData":[TD([[makeQuery(id+"F0.imprint","IMPRINT",EDGE,{"disambiguationData":[TD([[subQ5,-1.0]])],"derivedFrom":subQ3}),1.0]])]});}
            var Q44;
            {var subQ1=sQuery(id+"F0.wireOp",EDGE,"E4.2.2");var subQ3=sQuery(id+"F0.wireOp",EDGE,"E4.2.1");var subQ5=makeQuery(id+"F0.imprint","INTERSECT",VERTEX,{"derivedFrom":[subQ3,subQ1]});Q44=makeQuery(id+"F0.imprint","IMPRINT",FACE,{"disambiguationData":[TD([[makeQuery(id+"F0.imprint","IMPRINT",EDGE,{"disambiguationData":[TD([[subQ5,-1.0]])],"derivedFrom":subQ3}),-1.0]])]});}
            var Q45;
            {var subQ1=sQuery(id+"F0.wireOp",EDGE,"E4.3.2");var subQ3=sQuery(id+"F0.wireOp",EDGE,"E4.3.0");var subQ5=makeQuery(id+"F0.imprint","INTERSECT",VERTEX,{"derivedFrom":[subQ3,subQ1]});Q45=makeQuery(id+"F0.imprint","IMPRINT",FACE,{"disambiguationData":[TD([[makeQuery(id+"F0.imprint","IMPRINT",EDGE,{"disambiguationData":[TD([[subQ5,-1.0]])],"derivedFrom":subQ3}),1.0]])]});}
            var Q46;
            {var subQ1=sQuery(id+"F0.wireOp",EDGE,"E2.left");var subQ3=sQuery(id+"F0.wireOp",EDGE,"E2.bottom");var subQ5=makeQuery(id+"F0.imprint","INTERSECT",VERTEX,{"derivedFrom":[subQ3,subQ1]});Q46=makeQuery(id+"F0.imprint","IMPRINT",FACE,{"disambiguationData":[TD([[makeQuery(id+"F0.imprint","IMPRINT",EDGE,{"disambiguationData":[TD([[subQ5,-1.0]])],"derivedFrom":subQ3}),-1.0]])]});}
            var Q47;
            {var subQ1=sQuery(id+"F0.wireOp",EDGE,"E4.6.2");var subQ3=sQuery(id+"F0.wireOp",EDGE,"E4.6.1");var subQ5=makeQuery(id+"F0.imprint","INTERSECT",VERTEX,{"derivedFrom":[subQ3,subQ1]});Q47=makeQuery(id+"F0.imprint","IMPRINT",FACE,{"disambiguationData":[TD([[makeQuery(id+"F0.imprint","IMPRINT",EDGE,{"disambiguationData":[TD([[subQ5,-1.0]])],"derivedFrom":subQ3}),-1.0]])]});}
            var Q48;
            {var subQ1=sQuery(id+"F0.wireOp",EDGE,"E0");var subQ3=sQuery(id+"F0.wireOp",EDGE,"E4.11.3");var subQ5=makeQuery(id+"F0.imprint","INTERSECT",VERTEX,{"derivedFrom":[subQ1,subQ3]});Q48=makeQuery(id+"F0.imprint","IMPRINT",FACE,{"disambiguationData":[TD([[makeQuery(id+"F0.imprint","IMPRINT",EDGE,{"disambiguationData":[TD([[subQ5,-1.0]])],"derivedFrom":subQ1}),-1.0]])]});}
            var Q49;
            {var subQ0=sQuery(id+"F0.wireOp",EDGE,"E7");var subQ3=sQuery(id+"F0.wireOp",EDGE,"E4.8.0");var subQ4=makeQuery(id+"F0.imprint","INTERSECT",VERTEX,{"derivedFrom":[subQ3,subQ0]});Q49=makeQuery(id+"F0.imprint","IMPRINT",FACE,{"disambiguationData":[TD([[makeQuery(id+"F0.imprint","IMPRINT",EDGE,{"disambiguationData":[TD([[subQ4,-1.0]])],"derivedFrom":subQ0}),1.0]])]});}
            var Q50;
            {var subQ1=sQuery(id+"F0.wireOp",EDGE,"E4.14.2");var subQ3=sQuery(id+"F0.wireOp",EDGE,"E4.14.1");var subQ5=makeQuery(id+"F0.imprint","INTERSECT",VERTEX,{"derivedFrom":[subQ3,subQ1]});Q50=makeQuery(id+"F0.imprint","IMPRINT",FACE,{"disambiguationData":[TD([[makeQuery(id+"F0.imprint","IMPRINT",EDGE,{"disambiguationData":[TD([[subQ5,-1.0]])],"derivedFrom":subQ3}),-1.0]])]});}
            var Q51;
            {var subQ1=sQuery(id+"F0.wireOp",EDGE,"E4.22.2");var subQ3=sQuery(id+"F0.wireOp",EDGE,"E4.22.1");var subQ5=makeQuery(id+"F0.imprint","INTERSECT",VERTEX,{"derivedFrom":[subQ3,subQ1]});Q51=makeQuery(id+"F0.imprint","IMPRINT",FACE,{"disambiguationData":[TD([[makeQuery(id+"F0.imprint","IMPRINT",EDGE,{"disambiguationData":[TD([[subQ5,-1.0]])],"derivedFrom":subQ3}),-1.0]])]});}
            var Q52;
            {var subQ1=sQuery(id+"F0.wireOp",EDGE,"E0");var subQ3=sQuery(id+"F0.wireOp",EDGE,"E4.19.3");var subQ5=makeQuery(id+"F0.imprint","INTERSECT",VERTEX,{"derivedFrom":[subQ1,subQ3]});Q52=makeQuery(id+"F0.imprint","IMPRINT",FACE,{"disambiguationData":[TD([[makeQuery(id+"F0.imprint","IMPRINT",EDGE,{"disambiguationData":[TD([[subQ5,-1.0]])],"derivedFrom":subQ1}),-1.0]])]});}
            var Q53;
            {var subQ0=sQuery(id+"F0.wireOp",EDGE,"E7");var subQ3=sQuery(id+"F0.wireOp",EDGE,"E4.10.0");var subQ4=makeQuery(id+"F0.imprint","INTERSECT",VERTEX,{"derivedFrom":[subQ3,subQ0]});Q53=makeQuery(id+"F0.imprint","IMPRINT",FACE,{"disambiguationData":[TD([[makeQuery(id+"F0.imprint","IMPRINT",EDGE,{"disambiguationData":[TD([[subQ4,-1.0]])],"derivedFrom":subQ0}),1.0]])]});}
            var Q54;
            {var subQ1=sQuery(id+"F0.wireOp",EDGE,"E0");var subQ3=sQuery(id+"F0.wireOp",EDGE,"E4.13.3");var subQ5=makeQuery(id+"F0.imprint","INTERSECT",VERTEX,{"derivedFrom":[subQ1,subQ3]});Q54=makeQuery(id+"F0.imprint","IMPRINT",FACE,{"disambiguationData":[TD([[makeQuery(id+"F0.imprint","IMPRINT",EDGE,{"disambiguationData":[TD([[subQ5,-1.0]])],"derivedFrom":subQ1}),-1.0]])]});}
            var Q55;
            {var subQ1=sQuery(id+"F0.wireOp",EDGE,"E0");var subQ3=sQuery(id+"F0.wireOp",EDGE,"E4.21.3");var subQ5=makeQuery(id+"F0.imprint","INTERSECT",VERTEX,{"derivedFrom":[subQ1,subQ3]});Q55=makeQuery(id+"F0.imprint","IMPRINT",FACE,{"disambiguationData":[TD([[makeQuery(id+"F0.imprint","IMPRINT",EDGE,{"disambiguationData":[TD([[subQ5,-1.0]])],"derivedFrom":subQ1}),-1.0]])]});}
            var Q56;
            {var subQ1=sQuery(id+"F0.wireOp",EDGE,"E4.15.2");var subQ3=sQuery(id+"F0.wireOp",EDGE,"E4.15.1");var subQ5=makeQuery(id+"F0.imprint","INTERSECT",VERTEX,{"derivedFrom":[subQ3,subQ1]});Q56=makeQuery(id+"F0.imprint","IMPRINT",FACE,{"disambiguationData":[TD([[makeQuery(id+"F0.imprint","IMPRINT",EDGE,{"disambiguationData":[TD([[subQ5,-1.0]])],"derivedFrom":subQ3}),-1.0]])]});}
            var Q57;
            {var subQ1=sQuery(id+"F0.wireOp",EDGE,"E4.23.2");var subQ3=sQuery(id+"F0.wireOp",EDGE,"E4.23.1");var subQ5=makeQuery(id+"F0.imprint","INTERSECT",VERTEX,{"derivedFrom":[subQ3,subQ1]});Q57=makeQuery(id+"F0.imprint","IMPRINT",FACE,{"disambiguationData":[TD([[makeQuery(id+"F0.imprint","IMPRINT",EDGE,{"disambiguationData":[TD([[subQ5,-1.0]])],"derivedFrom":subQ3}),-1.0]])]});}
            var Q58;
            {var subQ1=sQuery(id+"F0.wireOp",EDGE,"E4.7.2");var subQ3=sQuery(id+"F0.wireOp",EDGE,"E4.7.1");var subQ5=makeQuery(id+"F0.imprint","INTERSECT",VERTEX,{"derivedFrom":[subQ3,subQ1]});Q58=makeQuery(id+"F0.imprint","IMPRINT",FACE,{"disambiguationData":[TD([[makeQuery(id+"F0.imprint","IMPRINT",EDGE,{"disambiguationData":[TD([[subQ5,-1.0]])],"derivedFrom":subQ3}),-1.0]])]});}
            var Q59;
            {var subQ1=sQuery(id+"F0.wireOp",EDGE,"E4.11.2");var subQ3=sQuery(id+"F0.wireOp",EDGE,"E4.11.0");var subQ5=makeQuery(id+"F0.imprint","INTERSECT",VERTEX,{"derivedFrom":[subQ3,subQ1]});Q59=makeQuery(id+"F0.imprint","IMPRINT",FACE,{"disambiguationData":[TD([[makeQuery(id+"F0.imprint","IMPRINT",EDGE,{"disambiguationData":[TD([[subQ5,-1.0]])],"derivedFrom":subQ3}),1.0]])]});}
            var Q60;
            {var subQ1=sQuery(id+"F0.wireOp",EDGE,"E4.19.2");var subQ3=sQuery(id+"F0.wireOp",EDGE,"E4.19.0");var subQ5=makeQuery(id+"F0.imprint","INTERSECT",VERTEX,{"derivedFrom":[subQ3,subQ1]});Q60=makeQuery(id+"F0.imprint","IMPRINT",FACE,{"disambiguationData":[TD([[makeQuery(id+"F0.imprint","IMPRINT",EDGE,{"disambiguationData":[TD([[subQ5,-1.0]])],"derivedFrom":subQ3}),1.0]])]});}
            var Q61;
            {var subQ1=sQuery(id+"F0.wireOp",EDGE,"E0");var subQ3=sQuery(id+"F0.wireOp",EDGE,"E4.4.3");var subQ5=makeQuery(id+"F0.imprint","INTERSECT",VERTEX,{"derivedFrom":[subQ1,subQ3]});Q61=makeQuery(id+"F0.imprint","IMPRINT",FACE,{"disambiguationData":[TD([[makeQuery(id+"F0.imprint","IMPRINT",EDGE,{"disambiguationData":[TD([[subQ5,-1.0]])],"derivedFrom":subQ1}),-1.0]])]});}
            var Q62;
            {var subQ0=sQuery(id+"F0.wireOp",EDGE,"E7");var subQ3=sQuery(id+"F0.wireOp",EDGE,"E4.1.0");var subQ4=makeQuery(id+"F0.imprint","INTERSECT",VERTEX,{"derivedFrom":[subQ3,subQ0]});Q62=makeQuery(id+"F0.imprint","IMPRINT",FACE,{"disambiguationData":[TD([[makeQuery(id+"F0.imprint","IMPRINT",EDGE,{"disambiguationData":[TD([[subQ4,-1.0]])],"derivedFrom":subQ0}),1.0]])]});}
            var Q63;
            {var subQ0=sQuery(id+"F0.wireOp",EDGE,"E7");var subQ3=sQuery(id+"F0.wireOp",EDGE,"E2.left");var subQ4=makeQuery(id+"F0.imprint","INTERSECT",VERTEX,{"derivedFrom":[subQ3,subQ0]});Q63=makeQuery(id+"F0.imprint","IMPRINT",FACE,{"disambiguationData":[TD([[makeQuery(id+"F0.imprint","IMPRINT",EDGE,{"disambiguationData":[TD([[subQ4,-1.0]])],"derivedFrom":subQ0}),1.0]])]});}
            var Q64;
            {var subQ1=sQuery(id+"F0.wireOp",EDGE,"E0");var subQ3=sQuery(id+"F0.wireOp",EDGE,"E4.2.3");var subQ5=makeQuery(id+"F0.imprint","INTERSECT",VERTEX,{"derivedFrom":[subQ1,subQ3]});Q64=makeQuery(id+"F0.imprint","IMPRINT",FACE,{"disambiguationData":[TD([[makeQuery(id+"F0.imprint","IMPRINT",EDGE,{"disambiguationData":[TD([[subQ5,-1.0]])],"derivedFrom":subQ1}),-1.0]])]});}
            var Q65;
            {var subQ1=sQuery(id+"F0.wireOp",EDGE,"E4.14.2");var subQ3=sQuery(id+"F0.wireOp",EDGE,"E4.14.0");var subQ5=makeQuery(id+"F0.imprint","INTERSECT",VERTEX,{"derivedFrom":[subQ3,subQ1]});Q65=makeQuery(id+"F0.imprint","IMPRINT",FACE,{"disambiguationData":[TD([[makeQuery(id+"F0.imprint","IMPRINT",EDGE,{"disambiguationData":[TD([[subQ5,-1.0]])],"derivedFrom":subQ3}),1.0]])]});}
            var Q66;
            {var subQ1=sQuery(id+"F0.wireOp",EDGE,"E4.3.2");var subQ3=sQuery(id+"F0.wireOp",EDGE,"E4.3.1");var subQ5=makeQuery(id+"F0.imprint","INTERSECT",VERTEX,{"derivedFrom":[subQ3,subQ1]});Q66=makeQuery(id+"F0.imprint","IMPRINT",FACE,{"disambiguationData":[TD([[makeQuery(id+"F0.imprint","IMPRINT",EDGE,{"disambiguationData":[TD([[subQ5,-1.0]])],"derivedFrom":subQ3}),-1.0]])]});}
            var Q67;
            {var subQ1=sQuery(id+"F0.wireOp",EDGE,"E4.4.2");var subQ3=sQuery(id+"F0.wireOp",EDGE,"E4.4.0");var subQ5=makeQuery(id+"F0.imprint","INTERSECT",VERTEX,{"derivedFrom":[subQ3,subQ1]});Q67=makeQuery(id+"F0.imprint","IMPRINT",FACE,{"disambiguationData":[TD([[makeQuery(id+"F0.imprint","IMPRINT",EDGE,{"disambiguationData":[TD([[subQ5,-1.0]])],"derivedFrom":subQ3}),1.0]])]});}
            var Q68;
            {var subQ1=sQuery(id+"F0.wireOp",EDGE,"E4.18.2");var subQ3=sQuery(id+"F0.wireOp",EDGE,"E4.18.0");var subQ5=makeQuery(id+"F0.imprint","INTERSECT",VERTEX,{"derivedFrom":[subQ3,subQ1]});Q68=makeQuery(id+"F0.imprint","IMPRINT",FACE,{"disambiguationData":[TD([[makeQuery(id+"F0.imprint","IMPRINT",EDGE,{"disambiguationData":[TD([[subQ5,-1.0]])],"derivedFrom":subQ3}),1.0]])]});}
            var Q69;
            {var subQ1=sQuery(id+"F0.wireOp",EDGE,"E4.10.2");var subQ3=sQuery(id+"F0.wireOp",EDGE,"E4.10.0");var subQ5=makeQuery(id+"F0.imprint","INTERSECT",VERTEX,{"derivedFrom":[subQ3,subQ1]});Q69=makeQuery(id+"F0.imprint","IMPRINT",FACE,{"disambiguationData":[TD([[makeQuery(id+"F0.imprint","IMPRINT",EDGE,{"disambiguationData":[TD([[subQ5,-1.0]])],"derivedFrom":subQ3}),1.0]])]});}
            var Q70;
            {var subQ1=sQuery(id+"F0.wireOp",EDGE,"E4.18.2");var subQ3=sQuery(id+"F0.wireOp",EDGE,"E4.18.1");var subQ5=makeQuery(id+"F0.imprint","INTERSECT",VERTEX,{"derivedFrom":[subQ3,subQ1]});Q70=makeQuery(id+"F0.imprint","IMPRINT",FACE,{"disambiguationData":[TD([[makeQuery(id+"F0.imprint","IMPRINT",EDGE,{"disambiguationData":[TD([[subQ5,-1.0]])],"derivedFrom":subQ3}),-1.0]])]});}
            var Q71;
            {var subQ1=sQuery(id+"F0.wireOp",EDGE,"E4.10.2");var subQ3=sQuery(id+"F0.wireOp",EDGE,"E4.10.1");var subQ5=makeQuery(id+"F0.imprint","INTERSECT",VERTEX,{"derivedFrom":[subQ3,subQ1]});Q71=makeQuery(id+"F0.imprint","IMPRINT",FACE,{"disambiguationData":[TD([[makeQuery(id+"F0.imprint","IMPRINT",EDGE,{"disambiguationData":[TD([[subQ5,-1.0]])],"derivedFrom":subQ3}),-1.0]])]});}
            var Q72;
            {var subQ0=sQuery(id+"F0.wireOp",EDGE,"E7");var subQ3=sQuery(id+"F0.wireOp",EDGE,"E2.right");var subQ4=makeQuery(id+"F0.imprint","INTERSECT",VERTEX,{"derivedFrom":[subQ3,subQ0]});Q72=makeQuery(id+"F0.imprint","IMPRINT",FACE,{"disambiguationData":[TD([[makeQuery(id+"F0.imprint","IMPRINT",EDGE,{"disambiguationData":[TD([[subQ4,1.0]])],"derivedFrom":subQ0}),1.0]])]});}
            var Q73;
            {var subQ1=sQuery(id+"F0.wireOp",EDGE,"E0");var subQ3=sQuery(id+"F0.wireOp",EDGE,"E4.3.3");var subQ5=makeQuery(id+"F0.imprint","INTERSECT",VERTEX,{"derivedFrom":[subQ1,subQ3]});Q73=makeQuery(id+"F0.imprint","IMPRINT",FACE,{"disambiguationData":[TD([[makeQuery(id+"F0.imprint","IMPRINT",EDGE,{"disambiguationData":[TD([[subQ5,-1.0]])],"derivedFrom":subQ1}),-1.0]])]});}
            var Q74;
            {var subQ1=sQuery(id+"F0.wireOp",EDGE,"E0");var subQ3=sQuery(id+"F0.wireOp",EDGE,"E4.15.3");var subQ5=makeQuery(id+"F0.imprint","INTERSECT",VERTEX,{"derivedFrom":[subQ1,subQ3]});Q74=makeQuery(id+"F0.imprint","IMPRINT",FACE,{"disambiguationData":[TD([[makeQuery(id+"F0.imprint","IMPRINT",EDGE,{"disambiguationData":[TD([[subQ5,-1.0]])],"derivedFrom":subQ1}),-1.0]])]});}
            var Q75;
            {var subQ0=sQuery(id+"F0.wireOp",EDGE,"E7");var subQ3=sQuery(id+"F0.wireOp",EDGE,"E4.12.0");var subQ4=makeQuery(id+"F0.imprint","INTERSECT",VERTEX,{"derivedFrom":[subQ3,subQ0]});Q75=makeQuery(id+"F0.imprint","IMPRINT",FACE,{"disambiguationData":[TD([[makeQuery(id+"F0.imprint","IMPRINT",EDGE,{"disambiguationData":[TD([[subQ4,-1.0]])],"derivedFrom":subQ0}),1.0]])]});}
            var Q76;
            {var subQ1=sQuery(id+"F0.wireOp",EDGE,"E4.12.2");var subQ3=sQuery(id+"F0.wireOp",EDGE,"E4.12.0");var subQ5=makeQuery(id+"F0.imprint","INTERSECT",VERTEX,{"derivedFrom":[subQ3,subQ1]});Q76=makeQuery(id+"F0.imprint","IMPRINT",FACE,{"disambiguationData":[TD([[makeQuery(id+"F0.imprint","IMPRINT",EDGE,{"disambiguationData":[TD([[subQ5,-1.0]])],"derivedFrom":subQ3}),1.0]])]});}
            var Q77;
            {var subQ1=sQuery(id+"F0.wireOp",EDGE,"E0");var subQ3=sQuery(id+"F0.wireOp",EDGE,"E2.top");var subQ5=makeQuery(id+"F0.imprint","INTERSECT",VERTEX,{"derivedFrom":[subQ1,subQ3]});Q77=makeQuery(id+"F0.imprint","IMPRINT",FACE,{"disambiguationData":[TD([[makeQuery(id+"F0.imprint","IMPRINT",EDGE,{"disambiguationData":[TD([[subQ5,1.0]])],"derivedFrom":subQ1}),-1.0]])]});}
            var Q78;
            {var subQ1=sQuery(id+"F0.wireOp",EDGE,"E4.16.2");var subQ3=sQuery(id+"F0.wireOp",EDGE,"E4.16.1");var subQ5=makeQuery(id+"F0.imprint","INTERSECT",VERTEX,{"derivedFrom":[subQ3,subQ1]});Q78=makeQuery(id+"F0.imprint","IMPRINT",FACE,{"disambiguationData":[TD([[makeQuery(id+"F0.imprint","IMPRINT",EDGE,{"disambiguationData":[TD([[subQ5,-1.0]])],"derivedFrom":subQ3}),-1.0]])]});}
            var Q79;
            {var subQ1=sQuery(id+"F0.wireOp",EDGE,"E4.8.2");var subQ3=sQuery(id+"F0.wireOp",EDGE,"E4.8.1");var subQ5=makeQuery(id+"F0.imprint","INTERSECT",VERTEX,{"derivedFrom":[subQ3,subQ1]});Q79=makeQuery(id+"F0.imprint","IMPRINT",FACE,{"disambiguationData":[TD([[makeQuery(id+"F0.imprint","IMPRINT",EDGE,{"disambiguationData":[TD([[subQ5,-1.0]])],"derivedFrom":subQ3}),-1.0]])]});}
            var Q80;
            {var subQ0=sQuery(id+"F0.wireOp",EDGE,"E7");var subQ3=sQuery(id+"F0.wireOp",EDGE,"E4.11.0");var subQ4=makeQuery(id+"F0.imprint","INTERSECT",VERTEX,{"derivedFrom":[subQ3,subQ0]});Q80=makeQuery(id+"F0.imprint","IMPRINT",FACE,{"disambiguationData":[TD([[makeQuery(id+"F0.imprint","IMPRINT",EDGE,{"disambiguationData":[TD([[subQ4,-1.0]])],"derivedFrom":subQ0}),1.0]])]});}
            var Q81;
            {var subQ1=sQuery(id+"F0.wireOp",EDGE,"E0");var subQ3=sQuery(id+"F0.wireOp",EDGE,"E4.22.3");var subQ5=makeQuery(id+"F0.imprint","INTERSECT",VERTEX,{"derivedFrom":[subQ1,subQ3]});Q81=makeQuery(id+"F0.imprint","IMPRINT",FACE,{"disambiguationData":[TD([[makeQuery(id+"F0.imprint","IMPRINT",EDGE,{"disambiguationData":[TD([[subQ5,-1.0]])],"derivedFrom":subQ1}),-1.0]])]});}
            var Q82;
            {var subQ1=sQuery(id+"F0.wireOp",EDGE,"E0");var subQ3=sQuery(id+"F0.wireOp",EDGE,"E4.14.3");var subQ5=makeQuery(id+"F0.imprint","INTERSECT",VERTEX,{"derivedFrom":[subQ1,subQ3]});Q82=makeQuery(id+"F0.imprint","IMPRINT",FACE,{"disambiguationData":[TD([[makeQuery(id+"F0.imprint","IMPRINT",EDGE,{"disambiguationData":[TD([[subQ5,-1.0]])],"derivedFrom":subQ1}),-1.0]])]});}
            var Q83;
            {var subQ1=sQuery(id+"F0.wireOp",EDGE,"E4.16.2");var subQ3=sQuery(id+"F0.wireOp",EDGE,"E4.16.0");var subQ5=makeQuery(id+"F0.imprint","INTERSECT",VERTEX,{"derivedFrom":[subQ3,subQ1]});Q83=makeQuery(id+"F0.imprint","IMPRINT",FACE,{"disambiguationData":[TD([[makeQuery(id+"F0.imprint","IMPRINT",EDGE,{"disambiguationData":[TD([[subQ5,-1.0]])],"derivedFrom":subQ3}),1.0]])]});}
            var Q84;
            {var subQ1=sQuery(id+"F0.wireOp",EDGE,"E0");var subQ3=sQuery(id+"F0.wireOp",EDGE,"E4.1.3");var subQ5=makeQuery(id+"F0.imprint","INTERSECT",VERTEX,{"derivedFrom":[subQ1,subQ3]});Q84=makeQuery(id+"F0.imprint","IMPRINT",FACE,{"disambiguationData":[TD([[makeQuery(id+"F0.imprint","IMPRINT",EDGE,{"disambiguationData":[TD([[subQ5,-1.0]])],"derivedFrom":subQ1}),-1.0]])]});}
            var Q85;
            {var subQ1=sQuery(id+"F0.wireOp",EDGE,"E4.8.2");var subQ3=sQuery(id+"F0.wireOp",EDGE,"E4.8.0");var subQ5=makeQuery(id+"F0.imprint","INTERSECT",VERTEX,{"derivedFrom":[subQ3,subQ1]});Q85=makeQuery(id+"F0.imprint","IMPRINT",FACE,{"disambiguationData":[TD([[makeQuery(id+"F0.imprint","IMPRINT",EDGE,{"disambiguationData":[TD([[subQ5,-1.0]])],"derivedFrom":subQ3}),1.0]])]});}
            var Q86;
            {var subQ0=sQuery(id+"F0.wireOp",EDGE,"E4.18.3");var subQ1=sQuery(id+"F0.wireOp",EDGE,"E0");var subQ2=makeQuery(id+"F0.imprint","INTERSECT",VERTEX,{"derivedFrom":[subQ1,subQ0]});Q86=makeQuery(id+"F0.imprint","IMPRINT",FACE,{"disambiguationData":[TD([[makeQuery(id+"F0.imprint","IMPRINT",EDGE,{"disambiguationData":[TD([[subQ2,1.0]])],"derivedFrom":subQ1}),-1.0]])]});}
            var Q87;
            {var subQ1=sQuery(id+"F0.wireOp",EDGE,"E4.9.2");var subQ3=sQuery(id+"F0.wireOp",EDGE,"E4.9.1");var subQ5=makeQuery(id+"F0.imprint","INTERSECT",VERTEX,{"derivedFrom":[subQ3,subQ1]});Q87=makeQuery(id+"F0.imprint","IMPRINT",FACE,{"disambiguationData":[TD([[makeQuery(id+"F0.imprint","IMPRINT",EDGE,{"disambiguationData":[TD([[subQ5,-1.0]])],"derivedFrom":subQ3}),-1.0]])]});}
            var Q88;
            {var subQ1=sQuery(id+"F0.wireOp",EDGE,"E4.17.2");var subQ3=sQuery(id+"F0.wireOp",EDGE,"E4.17.1");var subQ5=makeQuery(id+"F0.imprint","INTERSECT",VERTEX,{"derivedFrom":[subQ3,subQ1]});Q88=makeQuery(id+"F0.imprint","IMPRINT",FACE,{"disambiguationData":[TD([[makeQuery(id+"F0.imprint","IMPRINT",EDGE,{"disambiguationData":[TD([[subQ5,-1.0]])],"derivedFrom":subQ3}),-1.0]])]});}
            var Q89;
            {var subQ1=sQuery(id+"F0.wireOp",EDGE,"E0");var subQ3=sQuery(id+"F0.wireOp",EDGE,"E4.16.3");var subQ5=makeQuery(id+"F0.imprint","INTERSECT",VERTEX,{"derivedFrom":[subQ1,subQ3]});Q89=makeQuery(id+"F0.imprint","IMPRINT",FACE,{"disambiguationData":[TD([[makeQuery(id+"F0.imprint","IMPRINT",EDGE,{"disambiguationData":[TD([[subQ5,-1.0]])],"derivedFrom":subQ1}),-1.0]])]});}
            var Q90;
            {var subQ1=sQuery(id+"F0.wireOp",EDGE,"E4.20.2");var subQ3=sQuery(id+"F0.wireOp",EDGE,"E4.20.0");var subQ5=makeQuery(id+"F0.imprint","INTERSECT",VERTEX,{"derivedFrom":[subQ3,subQ1]});Q90=makeQuery(id+"F0.imprint","IMPRINT",FACE,{"disambiguationData":[TD([[makeQuery(id+"F0.imprint","IMPRINT",EDGE,{"disambiguationData":[TD([[subQ5,-1.0]])],"derivedFrom":subQ3}),1.0]])]});}
            var Q91;
            {var subQ1=sQuery(id+"F0.wireOp",EDGE,"E4.9.2");var subQ3=sQuery(id+"F0.wireOp",EDGE,"E4.9.0");var subQ5=makeQuery(id+"F0.imprint","INTERSECT",VERTEX,{"derivedFrom":[subQ3,subQ1]});Q91=makeQuery(id+"F0.imprint","IMPRINT",FACE,{"disambiguationData":[TD([[makeQuery(id+"F0.imprint","IMPRINT",EDGE,{"disambiguationData":[TD([[subQ5,-1.0]])],"derivedFrom":subQ3}),1.0]])]});}
            var Q92;
            {var subQ0=sQuery(id+"F0.wireOp",EDGE,"E7");var subQ3=sQuery(id+"F0.wireOp",EDGE,"E4.13.0");var subQ4=makeQuery(id+"F0.imprint","INTERSECT",VERTEX,{"derivedFrom":[subQ3,subQ0]});Q92=makeQuery(id+"F0.imprint","IMPRINT",FACE,{"disambiguationData":[TD([[makeQuery(id+"F0.imprint","IMPRINT",EDGE,{"disambiguationData":[TD([[subQ4,-1.0]])],"derivedFrom":subQ0}),1.0]])]});}
            var Q93;
            {var subQ1=sQuery(id+"F0.wireOp",EDGE,"E4.17.2");var subQ3=sQuery(id+"F0.wireOp",EDGE,"E4.17.0");var subQ5=makeQuery(id+"F0.imprint","INTERSECT",VERTEX,{"derivedFrom":[subQ3,subQ1]});Q93=makeQuery(id+"F0.imprint","IMPRINT",FACE,{"disambiguationData":[TD([[makeQuery(id+"F0.imprint","IMPRINT",EDGE,{"disambiguationData":[TD([[subQ5,-1.0]])],"derivedFrom":subQ3}),1.0]])]});}
            var Q94;
            {var subQ1=sQuery(id+"F0.wireOp",EDGE,"E4.23.2");var subQ3=sQuery(id+"F0.wireOp",EDGE,"E4.23.0");var subQ5=makeQuery(id+"F0.imprint","INTERSECT",VERTEX,{"derivedFrom":[subQ3,subQ1]});Q94=makeQuery(id+"F0.imprint","IMPRINT",FACE,{"disambiguationData":[TD([[makeQuery(id+"F0.imprint","IMPRINT",EDGE,{"disambiguationData":[TD([[subQ5,-1.0]])],"derivedFrom":subQ3}),1.0]])]});}
            var Q95;
            {var subQ1=sQuery(id+"F0.wireOp",EDGE,"E4.15.2");var subQ3=sQuery(id+"F0.wireOp",EDGE,"E4.15.0");var subQ5=makeQuery(id+"F0.imprint","INTERSECT",VERTEX,{"derivedFrom":[subQ3,subQ1]});Q95=makeQuery(id+"F0.imprint","IMPRINT",FACE,{"disambiguationData":[TD([[makeQuery(id+"F0.imprint","IMPRINT",EDGE,{"disambiguationData":[TD([[subQ5,-1.0]])],"derivedFrom":subQ3}),1.0]])]});}
            var Q96;
            {var subQ1=sQuery(id+"F0.wireOp",EDGE,"E4.7.2");var subQ3=sQuery(id+"F0.wireOp",EDGE,"E4.7.0");var subQ5=makeQuery(id+"F0.imprint","INTERSECT",VERTEX,{"derivedFrom":[subQ3,subQ1]});Q96=makeQuery(id+"F0.imprint","IMPRINT",FACE,{"disambiguationData":[TD([[makeQuery(id+"F0.imprint","IMPRINT",EDGE,{"disambiguationData":[TD([[subQ5,-1.0]])],"derivedFrom":subQ3}),1.0]])]});}
            var Q97;
            {var subQ1=sQuery(id+"F0.wireOp",EDGE,"E0");var subQ3=sQuery(id+"F0.wireOp",EDGE,"E4.20.3");var subQ5=makeQuery(id+"F0.imprint","INTERSECT",VERTEX,{"derivedFrom":[subQ1,subQ3]});Q97=makeQuery(id+"F0.imprint","IMPRINT",FACE,{"disambiguationData":[TD([[makeQuery(id+"F0.imprint","IMPRINT",EDGE,{"disambiguationData":[TD([[subQ5,-1.0]])],"derivedFrom":subQ1}),-1.0]])]});}
            var Q98;
            {var subQ1=sQuery(id+"F0.wireOp",EDGE,"E4.5.2");var subQ3=sQuery(id+"F0.wireOp",EDGE,"E4.5.1");var subQ5=makeQuery(id+"F0.imprint","INTERSECT",VERTEX,{"derivedFrom":[subQ3,subQ1]});Q98=makeQuery(id+"F0.imprint","IMPRINT",FACE,{"disambiguationData":[TD([[makeQuery(id+"F0.imprint","IMPRINT",EDGE,{"disambiguationData":[TD([[subQ5,-1.0]])],"derivedFrom":subQ3}),-1.0]])]});}
            var Q99;
            {var subQ1=sQuery(id+"F0.wireOp",EDGE,"E0");var subQ3=sQuery(id+"F0.wireOp",EDGE,"E4.12.3");var subQ5=makeQuery(id+"F0.imprint","INTERSECT",VERTEX,{"derivedFrom":[subQ1,subQ3]});Q99=makeQuery(id+"F0.imprint","IMPRINT",FACE,{"disambiguationData":[TD([[makeQuery(id+"F0.imprint","IMPRINT",EDGE,{"disambiguationData":[TD([[subQ5,-1.0]])],"derivedFrom":subQ1}),-1.0]])]});}
            var Q100;
            {var subQ1=sQuery(id+"F0.wireOp",EDGE,"E4.13.2");var subQ3=sQuery(id+"F0.wireOp",EDGE,"E4.13.0");var subQ5=makeQuery(id+"F0.imprint","INTERSECT",VERTEX,{"derivedFrom":[subQ3,subQ1]});Q100=makeQuery(id+"F0.imprint","IMPRINT",FACE,{"disambiguationData":[TD([[makeQuery(id+"F0.imprint","IMPRINT",EDGE,{"disambiguationData":[TD([[subQ5,-1.0]])],"derivedFrom":subQ3}),1.0]])]});}
            var Q101;
            {var subQ1=sQuery(id+"F0.wireOp",EDGE,"E4.21.2");var subQ3=sQuery(id+"F0.wireOp",EDGE,"E4.21.0");var subQ5=makeQuery(id+"F0.imprint","INTERSECT",VERTEX,{"derivedFrom":[subQ3,subQ1]});Q101=makeQuery(id+"F0.imprint","IMPRINT",FACE,{"disambiguationData":[TD([[makeQuery(id+"F0.imprint","IMPRINT",EDGE,{"disambiguationData":[TD([[subQ5,-1.0]])],"derivedFrom":subQ3}),1.0]])]});}
            var Q102;
            {var subQ1=sQuery(id+"F0.wireOp",EDGE,"E4.5.2");var subQ3=sQuery(id+"F0.wireOp",EDGE,"E4.5.0");var subQ5=makeQuery(id+"F0.imprint","INTERSECT",VERTEX,{"derivedFrom":[subQ3,subQ1]});Q102=makeQuery(id+"F0.imprint","IMPRINT",FACE,{"disambiguationData":[TD([[makeQuery(id+"F0.imprint","IMPRINT",EDGE,{"disambiguationData":[TD([[subQ5,-1.0]])],"derivedFrom":subQ3}),1.0]])]});}
            var Q103;
            {var subQ0=sQuery(id+"F0.wireOp",EDGE,"E7");var subQ3=sQuery(id+"F0.wireOp",EDGE,"E4.7.0");var subQ4=makeQuery(id+"F0.imprint","INTERSECT",VERTEX,{"derivedFrom":[subQ3,subQ0]});Q103=makeQuery(id+"F0.imprint","IMPRINT",FACE,{"disambiguationData":[TD([[makeQuery(id+"F0.imprint","IMPRINT",EDGE,{"disambiguationData":[TD([[subQ4,-1.0]])],"derivedFrom":subQ0}),1.0]])]});}
            var Q104;
            {var subQ1=sQuery(id+"F0.wireOp",EDGE,"E4.21.2");var subQ3=sQuery(id+"F0.wireOp",EDGE,"E4.21.1");var subQ5=makeQuery(id+"F0.imprint","INTERSECT",VERTEX,{"derivedFrom":[subQ3,subQ1]});Q104=makeQuery(id+"F0.imprint","IMPRINT",FACE,{"disambiguationData":[TD([[makeQuery(id+"F0.imprint","IMPRINT",EDGE,{"disambiguationData":[TD([[subQ5,-1.0]])],"derivedFrom":subQ3}),-1.0]])]});}
            var Q105;
            {var subQ0=sQuery(id+"F0.wireOp",EDGE,"E7");var subQ3=sQuery(id+"F0.wireOp",EDGE,"E4.5.0");var subQ4=makeQuery(id+"F0.imprint","INTERSECT",VERTEX,{"derivedFrom":[subQ3,subQ0]});Q105=makeQuery(id+"F0.imprint","IMPRINT",FACE,{"disambiguationData":[TD([[makeQuery(id+"F0.imprint","IMPRINT",EDGE,{"disambiguationData":[TD([[subQ4,-1.0]])],"derivedFrom":subQ0}),1.0]])]});}
            var Q106;
            {var subQ1=sQuery(id+"F0.wireOp",EDGE,"E4.19.2");var subQ3=sQuery(id+"F0.wireOp",EDGE,"E4.19.1");var subQ5=makeQuery(id+"F0.imprint","INTERSECT",VERTEX,{"derivedFrom":[subQ3,subQ1]});Q106=makeQuery(id+"F0.imprint","IMPRINT",FACE,{"disambiguationData":[TD([[makeQuery(id+"F0.imprint","IMPRINT",EDGE,{"disambiguationData":[TD([[subQ5,-1.0]])],"derivedFrom":subQ3}),-1.0]])]});}
            var Q107;
            {var subQ0=sQuery(id+"F0.wireOp",EDGE,"E7");var subQ3=sQuery(id+"F0.wireOp",EDGE,"E4.18.0");var subQ4=makeQuery(id+"F0.imprint","INTERSECT",VERTEX,{"derivedFrom":[subQ3,subQ0]});Q107=makeQuery(id+"F0.imprint","IMPRINT",FACE,{"disambiguationData":[TD([[makeQuery(id+"F0.imprint","IMPRINT",EDGE,{"disambiguationData":[TD([[subQ4,-1.0]])],"derivedFrom":subQ0}),1.0]])]});}
            var Q108;
            {var subQ1=sQuery(id+"F0.wireOp",EDGE,"E0");var subQ3=sQuery(id+"F0.wireOp",EDGE,"E4.5.3");var subQ5=makeQuery(id+"F0.imprint","INTERSECT",VERTEX,{"derivedFrom":[subQ1,subQ3]});Q108=makeQuery(id+"F0.imprint","IMPRINT",FACE,{"disambiguationData":[TD([[makeQuery(id+"F0.imprint","IMPRINT",EDGE,{"disambiguationData":[TD([[subQ5,-1.0]])],"derivedFrom":subQ1}),-1.0]])]});}
            var Q109;
            {var subQ1=sQuery(id+"F0.wireOp",EDGE,"E4.12.2");var subQ3=sQuery(id+"F0.wireOp",EDGE,"E4.12.1");var subQ5=makeQuery(id+"F0.imprint","INTERSECT",VERTEX,{"derivedFrom":[subQ3,subQ1]});Q109=makeQuery(id+"F0.imprint","IMPRINT",FACE,{"disambiguationData":[TD([[makeQuery(id+"F0.imprint","IMPRINT",EDGE,{"disambiguationData":[TD([[subQ5,-1.0]])],"derivedFrom":subQ3}),-1.0]])]});}
            var Q110;
            {var subQ1=sQuery(id+"F0.wireOp",EDGE,"E4.11.2");var subQ3=sQuery(id+"F0.wireOp",EDGE,"E4.11.1");var subQ5=makeQuery(id+"F0.imprint","INTERSECT",VERTEX,{"derivedFrom":[subQ3,subQ1]});Q110=makeQuery(id+"F0.imprint","IMPRINT",FACE,{"disambiguationData":[TD([[makeQuery(id+"F0.imprint","IMPRINT",EDGE,{"disambiguationData":[TD([[subQ5,-1.0]])],"derivedFrom":subQ3}),-1.0]])]});}
            var Q111;
            {var subQ0=sQuery(id+"F0.wireOp",EDGE,"E7");var subQ3=sQuery(id+"F0.wireOp",EDGE,"E4.21.0");var subQ4=makeQuery(id+"F0.imprint","INTERSECT",VERTEX,{"derivedFrom":[subQ3,subQ0]});Q111=makeQuery(id+"F0.imprint","IMPRINT",FACE,{"disambiguationData":[TD([[makeQuery(id+"F0.imprint","IMPRINT",EDGE,{"disambiguationData":[TD([[subQ4,-1.0]])],"derivedFrom":subQ0}),1.0]])]});}
            var Q112;
            {var subQ1=sQuery(id+"F0.wireOp",EDGE,"E0");var subQ3=sQuery(id+"F0.wireOp",EDGE,"E4.9.3");var subQ5=makeQuery(id+"F0.imprint","INTERSECT",VERTEX,{"derivedFrom":[subQ1,subQ3]});Q112=makeQuery(id+"F0.imprint","IMPRINT",FACE,{"disambiguationData":[TD([[makeQuery(id+"F0.imprint","IMPRINT",EDGE,{"disambiguationData":[TD([[subQ5,-1.0]])],"derivedFrom":subQ1}),-1.0]])]});}
            var Q113;
            {var subQ1=sQuery(id+"F0.wireOp",EDGE,"E0");var subQ3=sQuery(id+"F0.wireOp",EDGE,"E4.6.3");var subQ5=makeQuery(id+"F0.imprint","INTERSECT",VERTEX,{"derivedFrom":[subQ1,subQ3]});Q113=makeQuery(id+"F0.imprint","IMPRINT",FACE,{"disambiguationData":[TD([[makeQuery(id+"F0.imprint","IMPRINT",EDGE,{"disambiguationData":[TD([[subQ5,-1.0]])],"derivedFrom":subQ1}),-1.0]])]});}
            var Q114;
            {var subQ1=sQuery(id+"F0.wireOp",EDGE,"E4.13.2");var subQ3=sQuery(id+"F0.wireOp",EDGE,"E4.13.1");var subQ5=makeQuery(id+"F0.imprint","INTERSECT",VERTEX,{"derivedFrom":[subQ3,subQ1]});Q114=makeQuery(id+"F0.imprint","IMPRINT",FACE,{"disambiguationData":[TD([[makeQuery(id+"F0.imprint","IMPRINT",EDGE,{"disambiguationData":[TD([[subQ5,-1.0]])],"derivedFrom":subQ3}),-1.0]])]});}
            var Q115;
            {var subQ1=sQuery(id+"F0.wireOp",EDGE,"E0");var subQ3=sQuery(id+"F0.wireOp",EDGE,"E4.8.3");var subQ5=makeQuery(id+"F0.imprint","INTERSECT",VERTEX,{"derivedFrom":[subQ1,subQ3]});Q115=makeQuery(id+"F0.imprint","IMPRINT",FACE,{"disambiguationData":[TD([[makeQuery(id+"F0.imprint","IMPRINT",EDGE,{"disambiguationData":[TD([[subQ5,-1.0]])],"derivedFrom":subQ1}),-1.0]])]});}
            var Q116;
            {var subQ1=sQuery(id+"F0.wireOp",EDGE,"E0");var subQ3=sQuery(id+"F0.wireOp",EDGE,"E4.7.3");var subQ5=makeQuery(id+"F0.imprint","INTERSECT",VERTEX,{"derivedFrom":[subQ1,subQ3]});Q116=makeQuery(id+"F0.imprint","IMPRINT",FACE,{"disambiguationData":[TD([[makeQuery(id+"F0.imprint","IMPRINT",EDGE,{"disambiguationData":[TD([[subQ5,-1.0]])],"derivedFrom":subQ1}),-1.0]])]});}
            var Q117;
            {var subQ1=sQuery(id+"F0.wireOp",EDGE,"E4.20.2");var subQ3=sQuery(id+"F0.wireOp",EDGE,"E4.20.1");var subQ5=makeQuery(id+"F0.imprint","INTERSECT",VERTEX,{"derivedFrom":[subQ3,subQ1]});Q117=makeQuery(id+"F0.imprint","IMPRINT",FACE,{"disambiguationData":[TD([[makeQuery(id+"F0.imprint","IMPRINT",EDGE,{"disambiguationData":[TD([[subQ5,-1.0]])],"derivedFrom":subQ3}),-1.0]])]});}
            var Q118;
            {var subQ0=sQuery(id+"F0.wireOp",EDGE,"E7");var subQ3=sQuery(id+"F0.wireOp",EDGE,"E4.22.0");var subQ4=makeQuery(id+"F0.imprint","INTERSECT",VERTEX,{"derivedFrom":[subQ3,subQ0]});Q118=makeQuery(id+"F0.imprint","IMPRINT",FACE,{"disambiguationData":[TD([[makeQuery(id+"F0.imprint","IMPRINT",EDGE,{"disambiguationData":[TD([[subQ4,-1.0]])],"derivedFrom":subQ0}),1.0]])]});}
            var Q119;
            {var subQ1=sQuery(id+"F0.wireOp",EDGE,"E2.right");var subQ3=sQuery(id+"F0.wireOp",EDGE,"E2.bottom");var subQ5=makeQuery(id+"F0.imprint","INTERSECT",VERTEX,{"derivedFrom":[subQ3,subQ1]});Q119=makeQuery(id+"F0.imprint","IMPRINT",FACE,{"disambiguationData":[TD([[makeQuery(id+"F0.imprint","IMPRINT",EDGE,{"disambiguationData":[TD([[subQ5,1.0]])],"derivedFrom":subQ3}),-1.0]])]});}
            var Q120;
            {var subQ0=sQuery(id+"F0.wireOp",EDGE,"E4.19.3");var subQ1=sQuery(id+"F0.wireOp",EDGE,"E0");var subQ2=makeQuery(id+"F0.imprint","INTERSECT",VERTEX,{"derivedFrom":[subQ1,subQ0]});Q120=makeQuery(id+"F0.imprint","IMPRINT",FACE,{"disambiguationData":[TD([[makeQuery(id+"F0.imprint","IMPRINT",EDGE,{"disambiguationData":[TD([[subQ2,1.0]])],"derivedFrom":subQ1}),-1.0]])]});}
            var Q121;
            {var subQ1=sQuery(id+"F0.wireOp",EDGE,"E0");var subQ3=sQuery(id+"F0.wireOp",EDGE,"E2.top");var subQ5=makeQuery(id+"F0.imprint","INTERSECT",VERTEX,{"derivedFrom":[subQ1,subQ3]});Q121=makeQuery(id+"F0.imprint","IMPRINT",FACE,{"disambiguationData":[TD([[makeQuery(id+"F0.imprint","IMPRINT",EDGE,{"disambiguationData":[TD([[subQ5,-1.0]])],"derivedFrom":subQ1}),-1.0]])]});}
            extrude(context, id + "F1", {"entities" : qUnion([Q0, Q1, Q2, Q3, Q4, Q5, Q6, Q7, Q8, Q9, Q10, Q11, Q12, Q13, Q14, Q15, Q16, Q17, Q18, Q19, Q20, Q21, Q22, Q23, Q24, Q25, Q26, Q27, Q28, Q29, Q30, Q31, Q32, Q33, Q34, Q35, Q36, Q37, Q38, Q39, Q40, Q41, Q42, Q43, Q44, Q45, Q46, Q47, Q48, Q49, Q50, Q51, Q52, Q53, Q54, Q55, Q56, Q57, Q58, Q59, Q60, Q61, Q62, Q63, Q64, Q65, Q66, Q67, Q68, Q69, Q70, Q71, Q72, Q73, Q74, Q75, Q76, Q77, Q78, Q79, Q80, Q81, Q82, Q83, Q84, Q85, Q86, Q87, Q88, Q89, Q90, Q91, Q92, Q93, Q94, Q95, Q96, Q97, Q98, Q99, Q100, Q101, Q102, Q103, Q104, Q105, Q106, Q107, Q108, Q109, Q110, Q111, Q112, Q113, Q114, Q115, Q116, Q117, Q118, Q119, Q120, Q121]), "oppositeDirection" : true, "depth" : .7 * mm});
        }
        {
            var Q0;
            {var subQ40=sQuery(id+"F0.wireOp",EDGE,"E2.left");var subQ122=sQuery(id+"F0.wireOp",EDGE,"E2.bottom");var subQ171=makeQuery(id+"F0.imprint","INTERSECT",VERTEX,{"derivedFrom":[subQ122,subQ40]});Q0=makeQuery(id+"F0.imprint","IMPRINT",FACE,{"disambiguationData":[TD([[makeQuery(id+"F0.imprint","IMPRINT",EDGE,{"disambiguationData":[TD([[subQ171,-1.0]])],"derivedFrom":subQ122}),1.0]])]});}
            var Q1;
            {var subQ0=sQuery(id+"F0.wireOp",EDGE,"E7");var subQ3=sQuery(id+"F0.wireOp",EDGE,"E4.12.0");var subQ4=makeQuery(id+"F0.imprint","INTERSECT",VERTEX,{"derivedFrom":[subQ3,subQ0]});Q1=makeQuery(id+"F0.imprint","IMPRINT",FACE,{"disambiguationData":[TD([[makeQuery(id+"F0.imprint","IMPRINT",EDGE,{"disambiguationData":[TD([[subQ4,-1.0]])],"derivedFrom":subQ0}),1.0]])]});}
            var Q2;
            {var subQ0=sQuery(id+"F0.wireOp",EDGE,"E7");var subQ3=sQuery(id+"F0.wireOp",EDGE,"E4.11.0");var subQ4=makeQuery(id+"F0.imprint","INTERSECT",VERTEX,{"derivedFrom":[subQ3,subQ0]});Q2=makeQuery(id+"F0.imprint","IMPRINT",FACE,{"disambiguationData":[TD([[makeQuery(id+"F0.imprint","IMPRINT",EDGE,{"disambiguationData":[TD([[subQ4,-1.0]])],"derivedFrom":subQ0}),1.0]])]});}
            var Q3;
            {var subQ0=sQuery(id+"F0.wireOp",EDGE,"E7");var subQ3=sQuery(id+"F0.wireOp",EDGE,"E4.10.0");var subQ4=makeQuery(id+"F0.imprint","INTERSECT",VERTEX,{"derivedFrom":[subQ3,subQ0]});Q3=makeQuery(id+"F0.imprint","IMPRINT",FACE,{"disambiguationData":[TD([[makeQuery(id+"F0.imprint","IMPRINT",EDGE,{"disambiguationData":[TD([[subQ4,-1.0]])],"derivedFrom":subQ0}),1.0]])]});}
            var Q4;
            {var subQ0=sQuery(id+"F0.wireOp",EDGE,"E7");var subQ3=sQuery(id+"F0.wireOp",EDGE,"E4.9.0");var subQ4=makeQuery(id+"F0.imprint","INTERSECT",VERTEX,{"derivedFrom":[subQ3,subQ0]});Q4=makeQuery(id+"F0.imprint","IMPRINT",FACE,{"disambiguationData":[TD([[makeQuery(id+"F0.imprint","IMPRINT",EDGE,{"disambiguationData":[TD([[subQ4,-1.0]])],"derivedFrom":subQ0}),1.0]])]});}
            var Q5;
            {var subQ0=sQuery(id+"F0.wireOp",EDGE,"E7");var subQ3=sQuery(id+"F0.wireOp",EDGE,"E4.8.0");var subQ4=makeQuery(id+"F0.imprint","INTERSECT",VERTEX,{"derivedFrom":[subQ3,subQ0]});Q5=makeQuery(id+"F0.imprint","IMPRINT",FACE,{"disambiguationData":[TD([[makeQuery(id+"F0.imprint","IMPRINT",EDGE,{"disambiguationData":[TD([[subQ4,-1.0]])],"derivedFrom":subQ0}),1.0]])]});}
            var Q6;
            {var subQ0=sQuery(id+"F0.wireOp",EDGE,"E7");var subQ3=sQuery(id+"F0.wireOp",EDGE,"E4.13.0");var subQ4=makeQuery(id+"F0.imprint","INTERSECT",VERTEX,{"derivedFrom":[subQ3,subQ0]});Q6=makeQuery(id+"F0.imprint","IMPRINT",FACE,{"disambiguationData":[TD([[makeQuery(id+"F0.imprint","IMPRINT",EDGE,{"disambiguationData":[TD([[subQ4,-1.0]])],"derivedFrom":subQ0}),1.0]])]});}
            var Q7;
            Q7=makeQuery(id+"F0.imprint","IMPRINT",FACE,{"disambiguationData":[TD([[makeQuery(id+"F0.imprint","IMPRINT",EDGE,{"derivedFrom":sQuery(id+"F0.wireOp",EDGE,"E9.0")}),-1.0]])]});
            var Q8;
            {var subQ0=sQuery(id+"F0.wireOp",EDGE,"E7");var subQ3=sQuery(id+"F0.wireOp",EDGE,"E4.14.0");var subQ4=makeQuery(id+"F0.imprint","INTERSECT",VERTEX,{"derivedFrom":[subQ3,subQ0]});Q8=makeQuery(id+"F0.imprint","IMPRINT",FACE,{"disambiguationData":[TD([[makeQuery(id+"F0.imprint","IMPRINT",EDGE,{"disambiguationData":[TD([[subQ4,-1.0]])],"derivedFrom":subQ0}),1.0]])]});}
            var Q9;
            {var subQ0=sQuery(id+"F0.wireOp",EDGE,"E7");var subQ3=sQuery(id+"F0.wireOp",EDGE,"E4.15.0");var subQ4=makeQuery(id+"F0.imprint","INTERSECT",VERTEX,{"derivedFrom":[subQ3,subQ0]});Q9=makeQuery(id+"F0.imprint","IMPRINT",FACE,{"disambiguationData":[TD([[makeQuery(id+"F0.imprint","IMPRINT",EDGE,{"disambiguationData":[TD([[subQ4,-1.0]])],"derivedFrom":subQ0}),1.0]])]});}
            var Q10;
            {var subQ0=sQuery(id+"F0.wireOp",EDGE,"E7");var subQ3=sQuery(id+"F0.wireOp",EDGE,"E4.16.0");var subQ4=makeQuery(id+"F0.imprint","INTERSECT",VERTEX,{"derivedFrom":[subQ3,subQ0]});Q10=makeQuery(id+"F0.imprint","IMPRINT",FACE,{"disambiguationData":[TD([[makeQuery(id+"F0.imprint","IMPRINT",EDGE,{"disambiguationData":[TD([[subQ4,-1.0]])],"derivedFrom":subQ0}),1.0]])]});}
            var Q11;
            {var subQ0=sQuery(id+"F0.wireOp",EDGE,"E7");var subQ3=sQuery(id+"F0.wireOp",EDGE,"E4.17.0");var subQ4=makeQuery(id+"F0.imprint","INTERSECT",VERTEX,{"derivedFrom":[subQ3,subQ0]});Q11=makeQuery(id+"F0.imprint","IMPRINT",FACE,{"disambiguationData":[TD([[makeQuery(id+"F0.imprint","IMPRINT",EDGE,{"disambiguationData":[TD([[subQ4,-1.0]])],"derivedFrom":subQ0}),1.0]])]});}
            var Q12;
            {var subQ0=sQuery(id+"F0.wireOp",EDGE,"E7");var subQ3=sQuery(id+"F0.wireOp",EDGE,"E4.18.0");var subQ4=makeQuery(id+"F0.imprint","INTERSECT",VERTEX,{"derivedFrom":[subQ3,subQ0]});Q12=makeQuery(id+"F0.imprint","IMPRINT",FACE,{"disambiguationData":[TD([[makeQuery(id+"F0.imprint","IMPRINT",EDGE,{"disambiguationData":[TD([[subQ4,-1.0]])],"derivedFrom":subQ0}),1.0]])]});}
            var Q13;
            {var subQ0=sQuery(id+"F0.wireOp",EDGE,"E7");var subQ3=sQuery(id+"F0.wireOp",EDGE,"E4.19.0");var subQ4=makeQuery(id+"F0.imprint","INTERSECT",VERTEX,{"derivedFrom":[subQ3,subQ0]});Q13=makeQuery(id+"F0.imprint","IMPRINT",FACE,{"disambiguationData":[TD([[makeQuery(id+"F0.imprint","IMPRINT",EDGE,{"disambiguationData":[TD([[subQ4,-1.0]])],"derivedFrom":subQ0}),1.0]])]});}
            var Q14;
            {var subQ0=sQuery(id+"F0.wireOp",EDGE,"E7");var subQ3=sQuery(id+"F0.wireOp",EDGE,"E4.20.0");var subQ4=makeQuery(id+"F0.imprint","INTERSECT",VERTEX,{"derivedFrom":[subQ3,subQ0]});Q14=makeQuery(id+"F0.imprint","IMPRINT",FACE,{"disambiguationData":[TD([[makeQuery(id+"F0.imprint","IMPRINT",EDGE,{"disambiguationData":[TD([[subQ4,-1.0]])],"derivedFrom":subQ0}),1.0]])]});}
            var Q15;
            {var subQ0=sQuery(id+"F0.wireOp",EDGE,"E7");var subQ3=sQuery(id+"F0.wireOp",EDGE,"E4.21.0");var subQ4=makeQuery(id+"F0.imprint","INTERSECT",VERTEX,{"derivedFrom":[subQ3,subQ0]});Q15=makeQuery(id+"F0.imprint","IMPRINT",FACE,{"disambiguationData":[TD([[makeQuery(id+"F0.imprint","IMPRINT",EDGE,{"disambiguationData":[TD([[subQ4,-1.0]])],"derivedFrom":subQ0}),1.0]])]});}
            var Q16;
            {var subQ0=sQuery(id+"F0.wireOp",EDGE,"E7");var subQ3=sQuery(id+"F0.wireOp",EDGE,"E4.22.0");var subQ4=makeQuery(id+"F0.imprint","INTERSECT",VERTEX,{"derivedFrom":[subQ3,subQ0]});Q16=makeQuery(id+"F0.imprint","IMPRINT",FACE,{"disambiguationData":[TD([[makeQuery(id+"F0.imprint","IMPRINT",EDGE,{"disambiguationData":[TD([[subQ4,-1.0]])],"derivedFrom":subQ0}),1.0]])]});}
            var Q17;
            {var subQ0=sQuery(id+"F0.wireOp",EDGE,"E7");var subQ3=sQuery(id+"F0.wireOp",EDGE,"E2.right");var subQ4=makeQuery(id+"F0.imprint","INTERSECT",VERTEX,{"derivedFrom":[subQ3,subQ0]});Q17=makeQuery(id+"F0.imprint","IMPRINT",FACE,{"disambiguationData":[TD([[makeQuery(id+"F0.imprint","IMPRINT",EDGE,{"disambiguationData":[TD([[subQ4,1.0]])],"derivedFrom":subQ0}),1.0]])]});}
            var Q18;
            {var subQ0=sQuery(id+"F0.wireOp",EDGE,"E7");var subQ3=sQuery(id+"F0.wireOp",EDGE,"E2.left");var subQ4=makeQuery(id+"F0.imprint","INTERSECT",VERTEX,{"derivedFrom":[subQ3,subQ0]});Q18=makeQuery(id+"F0.imprint","IMPRINT",FACE,{"disambiguationData":[TD([[makeQuery(id+"F0.imprint","IMPRINT",EDGE,{"disambiguationData":[TD([[subQ4,-1.0]])],"derivedFrom":subQ0}),1.0]])]});}
            var Q19;
            {var subQ0=sQuery(id+"F0.wireOp",EDGE,"E7");var subQ3=sQuery(id+"F0.wireOp",EDGE,"E4.1.0");var subQ4=makeQuery(id+"F0.imprint","INTERSECT",VERTEX,{"derivedFrom":[subQ3,subQ0]});Q19=makeQuery(id+"F0.imprint","IMPRINT",FACE,{"disambiguationData":[TD([[makeQuery(id+"F0.imprint","IMPRINT",EDGE,{"disambiguationData":[TD([[subQ4,-1.0]])],"derivedFrom":subQ0}),1.0]])]});}
            var Q20;
            {var subQ0=sQuery(id+"F0.wireOp",EDGE,"E7");var subQ3=sQuery(id+"F0.wireOp",EDGE,"E4.3.0");var subQ4=makeQuery(id+"F0.imprint","INTERSECT",VERTEX,{"derivedFrom":[subQ3,subQ0]});Q20=makeQuery(id+"F0.imprint","IMPRINT",FACE,{"disambiguationData":[TD([[makeQuery(id+"F0.imprint","IMPRINT",EDGE,{"disambiguationData":[TD([[subQ4,-1.0]])],"derivedFrom":subQ0}),1.0]])]});}
            var Q21;
            {var subQ0=sQuery(id+"F0.wireOp",EDGE,"E7");var subQ3=sQuery(id+"F0.wireOp",EDGE,"E4.4.0");var subQ4=makeQuery(id+"F0.imprint","INTERSECT",VERTEX,{"derivedFrom":[subQ3,subQ0]});Q21=makeQuery(id+"F0.imprint","IMPRINT",FACE,{"disambiguationData":[TD([[makeQuery(id+"F0.imprint","IMPRINT",EDGE,{"disambiguationData":[TD([[subQ4,-1.0]])],"derivedFrom":subQ0}),1.0]])]});}
            var Q22;
            {var subQ0=sQuery(id+"F0.wireOp",EDGE,"E7");var subQ3=sQuery(id+"F0.wireOp",EDGE,"E4.5.0");var subQ4=makeQuery(id+"F0.imprint","INTERSECT",VERTEX,{"derivedFrom":[subQ3,subQ0]});Q22=makeQuery(id+"F0.imprint","IMPRINT",FACE,{"disambiguationData":[TD([[makeQuery(id+"F0.imprint","IMPRINT",EDGE,{"disambiguationData":[TD([[subQ4,-1.0]])],"derivedFrom":subQ0}),1.0]])]});}
            var Q23;
            {var subQ0=sQuery(id+"F0.wireOp",EDGE,"E7");var subQ3=sQuery(id+"F0.wireOp",EDGE,"E4.6.0");var subQ4=makeQuery(id+"F0.imprint","INTERSECT",VERTEX,{"derivedFrom":[subQ3,subQ0]});Q23=makeQuery(id+"F0.imprint","IMPRINT",FACE,{"disambiguationData":[TD([[makeQuery(id+"F0.imprint","IMPRINT",EDGE,{"disambiguationData":[TD([[subQ4,-1.0]])],"derivedFrom":subQ0}),1.0]])]});}
            var Q24;
            {var subQ0=sQuery(id+"F0.wireOp",EDGE,"E7");var subQ3=sQuery(id+"F0.wireOp",EDGE,"E4.7.0");var subQ4=makeQuery(id+"F0.imprint","INTERSECT",VERTEX,{"derivedFrom":[subQ3,subQ0]});Q24=makeQuery(id+"F0.imprint","IMPRINT",FACE,{"disambiguationData":[TD([[makeQuery(id+"F0.imprint","IMPRINT",EDGE,{"disambiguationData":[TD([[subQ4,-1.0]])],"derivedFrom":subQ0}),1.0]])]});}
            var Q25;
            {var subQ0=sQuery(id+"F0.wireOp",EDGE,"E7");var subQ3=sQuery(id+"F0.wireOp",EDGE,"E4.2.0");var subQ4=makeQuery(id+"F0.imprint","INTERSECT",VERTEX,{"derivedFrom":[subQ3,subQ0]});Q25=makeQuery(id+"F0.imprint","IMPRINT",FACE,{"disambiguationData":[TD([[makeQuery(id+"F0.imprint","IMPRINT",EDGE,{"disambiguationData":[TD([[subQ4,-1.0]])],"derivedFrom":subQ0}),1.0]])]});}
            extrude(context, id + "F2", {"entities" : qUnion([Q0, Q1, Q2, Q3, Q4, Q5, Q6, Q7, Q8, Q9, Q10, Q11, Q12, Q13, Q14, Q15, Q16, Q17, Q18, Q19, Q20, Q21, Q22, Q23, Q24, Q25]), "operationType" : NewBodyOperationType.ADD, "depth" : .7 * mm});
        }
        {
            var Q0;
            Q0=makeQuery(id+"F0.imprint","IMPRINT",FACE,{"disambiguationData":[TD([[makeQuery(id+"F0.imprint","IMPRINT",EDGE,{"derivedFrom":sQuery(id+"F0.wireOp",EDGE,"E11.0")}),-1.0]])]});
            extrude(context, id + "F3", {"entities" : qUnion([Q0]), "oppositeDirection" : true, "depth" : 10 * mm});
        }
        {
            var Q0;
            {var subQ1=sQuery(id+"F0.wireOp",EDGE,"E11.3");Q0=makeQuery(id+"F0.imprint","IMPRINT",FACE,{"disambiguationData":[TD([[makeQuery(id+"F0.imprint","IMPRINT",EDGE,{"derivedFrom":subQ1}),1.0]])]});}
            var Q1;
            {var subQ1=sQuery(id+"F0.wireOp",EDGE,"E11.2");Q1=makeQuery(id+"F0.imprint","IMPRINT",FACE,{"disambiguationData":[TD([[makeQuery(id+"F0.imprint","IMPRINT",EDGE,{"derivedFrom":subQ1}),1.0]])]});}
            var Q2;
            {var subQ1=sQuery(id+"F0.wireOp",EDGE,"E11.1");Q2=makeQuery(id+"F0.imprint","IMPRINT",FACE,{"disambiguationData":[TD([[makeQuery(id+"F0.imprint","IMPRINT",EDGE,{"derivedFrom":subQ1}),1.0]])]});}
            var Q3;
            {var subQ1=sQuery(id+"F0.wireOp",EDGE,"E11.0");Q3=makeQuery(id+"F0.imprint","IMPRINT",FACE,{"disambiguationData":[TD([[makeQuery(id+"F0.imprint","IMPRINT",EDGE,{"derivedFrom":subQ1}),1.0]])]});}
            var Q4;
            {var subQ1=sQuery(id+"F0.wireOp",EDGE,"E11.4");Q4=makeQuery(id+"F0.imprint","IMPRINT",FACE,{"disambiguationData":[TD([[makeQuery(id+"F0.imprint","IMPRINT",EDGE,{"derivedFrom":subQ1}),1.0]])]});}
            var Q5;
            {var subQ1=sQuery(id+"F0.wireOp",EDGE,"E11.5");Q5=makeQuery(id+"F0.imprint","IMPRINT",FACE,{"disambiguationData":[TD([[makeQuery(id+"F0.imprint","IMPRINT",EDGE,{"derivedFrom":subQ1}),1.0]])]});}
            var Q6;
            Q6=makeQuery(id+"F0.imprint","IMPRINT",FACE,{"disambiguationData":[TD([[makeQuery(id+"F0.imprint","IMPRINT",EDGE,{"derivedFrom":sQuery(id+"F0.wireOp",EDGE,"E11.0")}),-1.0]])]});
            extrude(context, id + "F4", {"entities" : qUnion([Q0, Q1, Q2, Q3, Q4, Q5, Q6]), "operationType" : NewBodyOperationType.ADD, "depth" : 45 * mm});
        }
        {
            var Q0;
            {var subQ1=sQuery(id+"F0.wireOp",EDGE,"E11.0");Q0=makeQuery(id+"F0.imprint","IMPRINT",FACE,{"disambiguationData":[TD([[makeQuery(id+"F0.imprint","IMPRINT",EDGE,{"derivedFrom":subQ1}),1.0]])]});}
            var Q1;
            {var subQ1=sQuery(id+"F0.wireOp",EDGE,"E11.5");Q1=makeQuery(id+"F0.imprint","IMPRINT",FACE,{"disambiguationData":[TD([[makeQuery(id+"F0.imprint","IMPRINT",EDGE,{"derivedFrom":subQ1}),1.0]])]});}
            var Q2;
            {var subQ1=sQuery(id+"F0.wireOp",EDGE,"E11.1");Q2=makeQuery(id+"F0.imprint","IMPRINT",FACE,{"disambiguationData":[TD([[makeQuery(id+"F0.imprint","IMPRINT",EDGE,{"derivedFrom":subQ1}),1.0]])]});}
            var Q3;
            {var subQ1=sQuery(id+"F0.wireOp",EDGE,"E11.2");Q3=makeQuery(id+"F0.imprint","IMPRINT",FACE,{"disambiguationData":[TD([[makeQuery(id+"F0.imprint","IMPRINT",EDGE,{"derivedFrom":subQ1}),1.0]])]});}
            var Q4;
            {var subQ1=sQuery(id+"F0.wireOp",EDGE,"E11.3");Q4=makeQuery(id+"F0.imprint","IMPRINT",FACE,{"disambiguationData":[TD([[makeQuery(id+"F0.imprint","IMPRINT",EDGE,{"derivedFrom":subQ1}),1.0]])]});}
            var Q5;
            {var subQ1=sQuery(id+"F0.wireOp",EDGE,"E11.4");Q5=makeQuery(id+"F0.imprint","IMPRINT",FACE,{"disambiguationData":[TD([[makeQuery(id+"F0.imprint","IMPRINT",EDGE,{"derivedFrom":subQ1}),1.0]])]});}
            extrude(context, id + "F5", {"entities" : qUnion([Q0, Q1, Q2, Q3, Q4, Q5]), "operationType" : NewBodyOperationType.REMOVE, "depth" : 45 * mm, "hasSecondDirection" : true, "secondDirectionOppositeDirection" : false, "secondDirectionDepth" : 35 * mm});
        }
    });
